FCSTD DOCUMENT  (FreeCAD 0.16RUnknown)
Label: Bioreactor_sketches_04
License: All rights reserved
LicenseURL: http://en.wikipedia.org/wiki/All_rights_reserved
objects: Sketcher::SketchObject×15, Spreadsheet::Sheet×1
note: 15 computed .brp shape members not serialized (recipe doc carries the construction recipe); baked Part::Feature solids carry a one-line shape summary decoded from their .brp

FEATURE [Spreadsheet::Sheet] Spreadsheet  label="prefs001"
  cells = A1=PCBHeated; B1(pcbheated)=214; C1=mm; D1=name=pcbheated; A2=Plexi thickness main; B2(plexi)=6; C2=mm; D2=name=plexi; A3=Plexi thickness LCD top; B3(plexi_LCDcover)=4; C3=mm; D3=name=plexi_LCDcover; E3=WARNING: cut in different plexi thickness; A4=Grande Encoche; B4(big_encoche)=75; C4=mm; D4=name=big_encoche; A5=Boite_LCD_to_side; B5(lcd2side)=34.5; C5=mm; D5=name=lcd2side; A6=Length LCD box; B6(lcd_length)=70; C6=mm; D6=name=lcd_length; A7=Encoche LCD; B7(lcd_encoche)=47; C7=mm; D7=name=lcd_encoche; A8=Encoche side; B8(side_encoche)=16; C8=mm; D8=name=side_encoche; A9=Encoche LCD side; B9(LCDside_encoche)=14; C9=mm; D9=name=LCDside_encoche; A10=Encoche LCD bottom; B10(LCDbottom_encoche)=47; C10=mm; D10=name=LCDbottom_encoche; A11=Encoche LCD cover length; B11(LCDcover_encoche)=128; C11=mm; D11=name=LCDcover_encoche; A12=Box height; B12(box_height)=58; C12=mm; D12=name=box_height; A13=Encoche top; B13(top_encoche)=45; C13=mm; D13=name=top_encoche; A14=Plug opening width; B14(plug_width)=90; C14=mm; D14=name=plug_width; A15=Plug opening height; B15(plug_height)=25; C15=mm; D15=name=plug_height; A16=Radius Pump; B16(radius_pump)==29 / 2; C16=mm; D16=name=radius_pump; A17=Radius pump screw; B17(radius_pump_screw)==4 / 2; C17=mm; D17=name=radius_pump_screw; A18=Radius stepper; B18(radius_stepper)=6; C18=mm; D18=name=radius_stepper; A19=Radius stepper screw; B19(radius_stepper_screw)=2; C19=mm; D19=name=radius_stepper_screw; A20=Diagonal distance between stepper screws; B20(stepper_screw_dist1)=44; C20=mm; D20=name=stepper_screw_dist1; A21=Load cell opening length; B21(load_length)=55; C21=mm; D21=name=load_length; A22=Load cell opening width; B22(load_width)=17; C22=mm; D22=name=load_width; A23=Radius load cell screw; B23(load_screw)=2.5; C23=mm; D23=name=load_screw; A24=Distance between load position screw; B24(load_dist1)=10; C24=mm; D24=name=load_dist1; E24=value for smaller loading cell = 5; A25=Distance between stepper & loading points; B25(load_dist_point)=67.5; C25=mm; D25=name=load_dist_point; A26=Distance load screw opening; B26(load_dist2)=7; C26=mm; D26=name=load_dist2; A27=Distance screw weighting; B27(load_dist_weight)==66 + 2.5; C27=mm; D27=name=load_dist_weight; E27=value for smaller loading cell = 62.5; A28=Load cell opening border distance; B28(load_border)=20; C28=mm; D28=name=load_border; A29=USB entry length; B29(usb_length)=9; C29=mm; D29=name=usb_length; A30=USB entry height; B30(usb_height)=5; C30=mm; D30=name=usb_height; A31=Ethernet entry length; B31(ethernet_length)=15; C31=mm; D31=name=ethernet_length; A32=Ethernet entry height; B32(ethernet_height)=16; C32=mm; D32=name=ethernet_height; A33=Power entry length; B33(power_length)=10; C33=mm; D33=name=power_length; A34=Power entry height; B34(power_height)=12.5; C34=mm; D34=name=power_height
FEATURE [Sketcher::SketchObject] Sketch  label="BASE_JUPE_MALE"
  expr: Constraints[17] = prefs001.pcbheated
  expr: Constraints[18] = prefs001.plexi * 2
  expr: Constraints[20] = prefs001.plexi * 2
  expr: Constraints[33] = prefs001.plexi * 2
  expr: Constraints[23] = prefs001.plexi * 2
  expr: Constraints[22] = prefs001.plexi
  expr: Constraints[24] = prefs001.plexi * 2
  expr: Constraints[35] = prefs001.pcbheated
  sketch-geometry (12):
    g0: LineSegment StartX=230 StartY=22 StartZ=0 EndX=236 EndY=22 EndZ=0
    g1: LineSegment StartX=236 StartY=22 StartZ=0 EndX=236 EndY=34 EndZ=0
    g2: LineSegment StartX=236 StartY=34 StartZ=0 EndX=230 EndY=34 EndZ=0
    g3: LineSegment StartX=230 StartY=34 StartZ=0 EndX=230 EndY=46 EndZ=0
    g4: LineSegment StartX=230 StartY=46 StartZ=0 EndX=16 EndY=46 EndZ=0
    g5: LineSegment StartX=16 StartY=46 StartZ=0 EndX=16 EndY=34 EndZ=0
    g6: LineSegment StartX=16 StartY=34 StartZ=0 EndX=10 EndY=34 EndZ=0
    g7: LineSegment StartX=10 StartY=34 StartZ=0 EndX=10 EndY=22 EndZ=0
    g8: LineSegment StartX=10 StartY=22 StartZ=0 EndX=16 EndY=22 EndZ=0
    g9: LineSegment StartX=16 StartY=22 StartZ=0 EndX=16 EndY=10 EndZ=0
    g10: LineSegment StartX=16 StartY=10 StartZ=0 EndX=230 EndY=10 EndZ=0
    g11: LineSegment StartX=230 StartY=10 StartZ=0 EndX=230 EndY=22 EndZ=0
  constraints (36):
    c: Horizontal(g0)
    c: Vertical(g1)
    c: Horizontal(g2)
    c: Vertical(g3)
    c: Horizontal(g4)
    c: Vertical(g5)
    c: Vertical(g7)
    c: DistanceX(g-1,g7) = 10
    c: Coincident(g7,g6)
    c: Coincident(g7,g8)
    c: Coincident(g0,g1)
    c: Coincident(g2,g1)
    c: Coincident(g2,g3)
    c: Coincident(g3,g4)
    c: Coincident(g5,g4)
    c: Coincident(g5,g6)
    c: Horizontal(g8)
    c: DistanceX(g4,g4) = 214
    c: DistanceY(g5,g5) = 12
    c: Horizontal(g6)
    c: DistanceY(g7,g7) = 12
    c: DistanceX(g8,g8) = 6
    c: DistanceX(g6,g6) = 6
    c: DistanceY(g3,g3) = 12
    c: DistanceY(g1,g1) = 12
    c: DistanceX(g2,g2) = 6
    c: Vertical(g9)
    c: Coincident(g9,g10)
    c: Horizontal(g10)
    c: Coincident(g10,g11)
    c: Coincident(g11,g0)
    c: Vertical(g11)
    c: Coincident(g9,g8)
    c: DistanceY(g9,g9) = 12
    c: DistanceY(g-1,g9) = 10
    c: DistanceX(g10,g10) = 214
FEATURE [Sketcher::SketchObject] Sketch001  label="BASE_JUPE_FEMELLE"
  expr: Constraints[37] = prefs001.plexi
  expr: Constraints[34] = prefs001.plexi * 2
  expr: Constraints[33] = prefs001.plexi * 2
  expr: Constraints[11] = prefs001.plexi
  expr: Constraints[36] = prefs001.plexi
  expr: Constraints[31] = prefs001.pcbheated + 2 * prefs001.plexi
  sketch-geometry (14):
    g0: LineSegment StartX=-236 StartY=27 StartZ=0 EndX=-230 EndY=27 EndZ=0
    g1: LineSegment StartX=-230 StartY=27 StartZ=0 EndX=-230 EndY=39 EndZ=0
    g2: LineSegment StartX=-230 StartY=39 StartZ=0 EndX=-236 EndY=39 EndZ=0
    g3: LineSegment StartX=-236 StartY=39 StartZ=0 EndX=-236 EndY=50 EndZ=0
    g4: LineSegment StartX=-196 StartY=90 StartZ=0 EndX=-50 EndY=90 EndZ=0
    g5: LineSegment StartX=-16 StartY=39 StartZ=0 EndX=-16 EndY=27 EndZ=0
    g6: ArcOfCircle CenterX=-50 CenterY=50 CenterZ=0 NormalX=0 NormalY=0 NormalZ=1 Radius=40 StartAngle=2.17158e-06 EndAngle=1.5708
    g7: ArcOfCircle CenterX=-196 CenterY=50 CenterZ=0 NormalX=0 NormalY=0 NormalZ=1 Radius=40 StartAngle=1.5708 EndAngle=3.14159
    g8: LineSegment StartX=-16 StartY=39 StartZ=0 EndX=-10 EndY=39 EndZ=0
    g9: LineSegment StartX=-10 StartY=50.0001 StartZ=0 EndX=-10 EndY=39 EndZ=0
    g10: LineSegment StartX=-236 StartY=27 StartZ=0 EndX=-236 EndY=15 EndZ=0
    g11: LineSegment StartX=-236 StartY=15 StartZ=0 EndX=-10 EndY=15 EndZ=0
    g12: LineSegment StartX=-10 StartY=15 StartZ=0 EndX=-10 EndY=27 EndZ=0
    g13: LineSegment StartX=-10 StartY=27 StartZ=0 EndX=-16 EndY=27 EndZ=0
  constraints (41):
    c: Horizontal(g0)
    c: Coincident(g0,g1)
    c: Vertical(g1)
    c: Coincident(g1,g2)
    c: Horizontal(g2)
    c: Coincident(g2,g3)
    c: Vertical(g3)
    c: Horizontal(g4)
    c: Vertical(g5)
    c: DistanceY(g1,g1) = 12
    c: DistanceY(g5,g5) = 12
    c: DistanceX(g2,g2) = 6
    c: DistanceX(g0,g0) = 6
    c: Tangent(g4,g6) = 1.5708
    c: Tangent(g3,g7) = 1.5708
    c: Tangent(g4,g7) = 1.5708
    c: Radius(g7) = 40
    c: Radius(g6) = 40
    c: Coincident(g8,g5)
    c: Horizontal(g8)
    c: Coincident(g9,g6)
    c: Coincident(g9,g8)
    c: Vertical(g9)
    c: Vertical(g10)
    c: Coincident(g10,g11)
    c: Horizontal(g11)
    c: Coincident(g11,g12)
    c: Vertical(g12)
    c: Coincident(g12,g13)
    c: Coincident(g13,g5)
    c: Horizontal(g13)
    c: DistanceX(g11,g11) = 226
    c: DistanceY(g10,g4) = 75
    c: DistanceY(g10,g10) = 12
    c: DistanceY(g12,g12) = 12
    c: Coincident(g0,g10)
    c: DistanceX(g8,g8) = 6
    c: DistanceX(g13,g13) = 6
    c: DistanceY(g-1,g11) = 15
    c: DistanceX(g11,g-1) = 10
    c: Tangent(g6,g9)
FEATURE [Sketcher::SketchObject] Sketch002  label="BASE_FOND"
  expr: Constraints[106] = 89.5 + 3.2
  expr: Constraints[83] = prefs001.lcd2side
  expr: Constraints[104] = 89.5 + 3.2
  expr: Constraints[97] = 51.5 + 3.2
  expr: Constraints[94] = (prefs001.pcbheated - 4 - prefs001.lcd_encoche - 2 * prefs001.lcd2side - 2 * prefs001.plexi) / 2
  expr: Constraints[91] = prefs001.plexi
  expr: Constraints[90] = prefs001.lcd_length / 2
  expr: Constraints[88] = prefs001.lcd_length / 2
  expr: Constraints[71] = prefs001.plexi
  expr: Constraints[57] = (prefs001.pcbheated - 4 - prefs001.big_encoche) / 2
  expr: Constraints[59] = prefs001.big_encoche
  expr: Constraints[65] = (prefs001.pcbheated - 4 - prefs001.big_encoche) / 2
  expr: Constraints[72] = prefs001.plexi
  expr: Constraints[64] = (prefs001.pcbheated - 4 - prefs001.big_encoche) / 2
  expr: Constraints[61] = prefs001.big_encoche
  expr: Constraints[117] = 9 + 6
  expr: Constraints[62] = (prefs001.pcbheated - 4 - prefs001.big_encoche) / 2
  expr: Constraints[89] = prefs001.lcd_length / 2
  expr: Constraints[66] = prefs001.big_encoche
  expr: Constraints[84] = prefs001.big_encoche
  expr: Constraints[68] = prefs001.plexi
  expr: Constraints[69] = prefs001.plexi
  expr: Constraints[73] = prefs001.plexi
  expr: Constraints[67] = prefs001.plexi
  expr: Constraints[85] = prefs001.plexi
  expr: Constraints[105] = 51.5 + 3.2
  expr: Constraints[82] = prefs001.lcd2side
  expr: Constraints[60] = (prefs001.pcbheated - 4 - prefs001.big_encoche) / 2
  expr: Constraints[93] = (prefs001.pcbheated - 4 - prefs001.lcd_encoche - 2 * prefs001.lcd2side - 2 * prefs001.plexi) / 2
  expr: Constraints[92] = prefs001.lcd_encoche
  expr: Constraints[87] = (prefs001.pcbheated - 4 - prefs001.big_encoche - 2 * prefs001.lcd2side) / 2
  expr: Constraints[58] = (prefs001.pcbheated - 4 - prefs001.big_encoche) / 2
  sketch-geometry (40):
    g0: LineSegment StartX=0 StartY=0 StartZ=0 EndX=0 EndY=-67.5 EndZ=0
    g1: LineSegment StartX=0 StartY=-67.5 StartZ=0 EndX=6 EndY=-67.5 EndZ=0
    g2: LineSegment StartX=6 StartY=-67.5 StartZ=0 EndX=6 EndY=-142.5 EndZ=0
    g3: LineSegment StartX=6 StartY=-142.5 StartZ=0 EndX=0 EndY=-142.5 EndZ=0
    g4: LineSegment StartX=0 StartY=-142.5 StartZ=0 EndX=0 EndY=-210 EndZ=0
    g5: LineSegment StartX=0 StartY=-210 StartZ=0 EndX=67.5 EndY=-210 EndZ=0
    g6: LineSegment StartX=67.5 StartY=-210 StartZ=0 EndX=67.5 EndY=-204 EndZ=0
    g7: LineSegment StartX=67.5 StartY=-204 StartZ=0 EndX=142.5 EndY=-204 EndZ=0
    g8: LineSegment StartX=142.5 StartY=-204 StartZ=0 EndX=142.5 EndY=-210 EndZ=0
    g9: LineSegment StartX=142.5 StartY=-210 StartZ=0 EndX=210 EndY=-210 EndZ=0
    g10: LineSegment StartX=210 StartY=-210 StartZ=0 EndX=210 EndY=-175.5 EndZ=0
    g11: LineSegment StartX=210 StartY=-175.5 StartZ=0 EndX=245 EndY=-175.5 EndZ=0
    g12: LineSegment StartX=245 StartY=-175.5 StartZ=0 EndX=245 EndY=-169.5 EndZ=0
    g13: LineSegment StartX=245 StartY=-169.5 StartZ=0 EndX=280 EndY=-169.5 EndZ=0
    g14: LineSegment StartX=280 StartY=-169.5 StartZ=0 EndX=280 EndY=-128.5 EndZ=0
    g15: LineSegment StartX=280 StartY=-128.5 StartZ=0 EndX=274 EndY=-128.5 EndZ=0
    g16: LineSegment StartX=274 StartY=-128.5 StartZ=0 EndX=274 EndY=-81.5 EndZ=0
    g17: LineSegment StartX=274 StartY=-81.5 StartZ=0 EndX=280 EndY=-81.5 EndZ=0
    g18: LineSegment StartX=280 StartY=-81.5 StartZ=0 EndX=280 EndY=-40.5 EndZ=0
    g19: LineSegment StartX=280 StartY=-40.5 StartZ=0 EndX=245 EndY=-40.5 EndZ=0
    g20: LineSegment StartX=245 StartY=-40.5 StartZ=0 EndX=245 EndY=-34.5 EndZ=0
    g21: LineSegment StartX=245 StartY=-34.5 StartZ=0 EndX=210 EndY=-34.5 EndZ=0
    g22: LineSegment StartX=210 StartY=-34.5 StartZ=0 EndX=210 EndY=0 EndZ=0
    g23: LineSegment StartX=210 StartY=0 StartZ=0 EndX=142.5 EndY=0 EndZ=0
    g24: LineSegment StartX=142.5 StartY=0 StartZ=0 EndX=142.5 EndY=-6 EndZ=0
    g25: LineSegment StartX=142.5 StartY=-6 StartZ=0 EndX=67.5 EndY=-6 EndZ=0
    g26: LineSegment StartX=67.5 StartY=-6 StartZ=0 EndX=67.5 EndY=0 EndZ=0
    g27: LineSegment StartX=67.5 StartY=0 StartZ=0 EndX=0 EndY=0 EndZ=0
    g28: LineSegment StartX=204 StartY=-67.5 StartZ=0 EndX=210 EndY=-67.5 EndZ=0
    g29: LineSegment StartX=210 StartY=-67.5 StartZ=0 EndX=210 EndY=-142.5 EndZ=0
    g30: LineSegment StartX=210 StartY=-142.5 StartZ=0 EndX=204 EndY=-142.5 EndZ=0
    g31: LineSegment StartX=204 StartY=-142.5 StartZ=0 EndX=204 EndY=-67.5 EndZ=0
    g32: Circle CenterX=269 CenterY=-165.5 CenterZ=0 NormalX=0 NormalY=0 NormalZ=1 Radius=1.6
    g33: Circle CenterX=214.3 CenterY=-165.5 CenterZ=0 NormalX=0 NormalY=0 NormalZ=1 Radius=1.6
    g34: Circle CenterX=214.3 CenterY=-72.8 CenterZ=0 NormalX=0 NormalY=0 NormalZ=1 Radius=1.6
    g35: Circle CenterX=269 CenterY=-72.8 CenterZ=0 NormalX=0 NormalY=0 NormalZ=1 Radius=1.6
    g36: Circle CenterX=15 CenterY=-190 CenterZ=0 NormalX=0 NormalY=0 NormalZ=1 Radius=1.6
    g37: Circle CenterX=88 CenterY=-190 CenterZ=0 NormalX=0 NormalY=0 NormalZ=1 Radius=1.6
    g38: Circle CenterX=88 CenterY=-96 CenterZ=0 NormalX=0 NormalY=0 NormalZ=1 Radius=1.6
    g39: Circle CenterX=15 CenterY=-96 CenterZ=0 NormalX=0 NormalY=0 NormalZ=1 Radius=1.6
  constraints (119):
    c: Coincident(g-1,g0)
    c: Vertical(g0)
    c: Coincident(g0,g1)
    c: Horizontal(g1)
    c: Coincident(g1,g2)
    c: Vertical(g2)
    c: Coincident(g2,g3)
    c: PointOnObject(g3,g-2)
    c: Horizontal(g3)
    c: Coincident(g3,g4)
    c: Vertical(g4)
    c: Coincident(g4,g5)
    c: Horizontal(g5)
    c: Coincident(g5,g6)
    c: Vertical(g6)
    c: Coincident(g6,g7)
    c: Horizontal(g7)
    c: Coincident(g7,g8)
    c: Vertical(g8)
    c: Coincident(g8,g9)
    c: Horizontal(g9)
    c: Coincident(g9,g10)
    c: Vertical(g10)
    c: Coincident(g10,g11)
    c: Horizontal(g11)
    c: Coincident(g11,g12)
    c: Vertical(g12)
    c: Coincident(g12,g13)
    c: Horizontal(g13)
    c: Coincident(g13,g14)
    c: Vertical(g14)
    c: Coincident(g14,g15)
    c: Horizontal(g15)
    c: Coincident(g15,g16)
    c: Vertical(g16)
    c: Coincident(g16,g17)
    c: Horizontal(g17)
    c: Coincident(g17,g18)
    c: Vertical(g18)
    c: Coincident(g18,g19)
    c: Horizontal(g19)
    c: Coincident(g19,g20)
    c: Vertical(g20)
    c: Coincident(g20,g21)
    c: Horizontal(g21)
    c: Coincident(g21,g22)
    c: Vertical(g22)
    c: Coincident(g22,g23)
    c: Horizontal(g23)
    c: Coincident(g23,g24)
    c: Coincident(g24,g25)
    c: Horizontal(g25)
    c: Coincident(g25,g26)
    c: Vertical(g26)
    c: Coincident(g26,g27)
    c: Coincident(g27,g0)
    c: Horizontal(g27)
    c: DistanceY(g0,g0) = 67.5
    c: DistanceY(g4,g4) = 67.5
    c: DistanceY(g2,g2) = 75
    c: DistanceX(g5,g5) = 67.5
    c: DistanceX(g7,g7) = 75
    c: DistanceX(g9,g9) = 67.5
    c: Vertical(g24)
    c: DistanceX(g23,g23) = 67.5
    c: DistanceX(g27,g27) = 67.5
    c: DistanceX(g25,g25) = 75
    c: DistanceY(g8,g8) = 6
    c: DistanceY(g6,g6) = 6
    c: DistanceX(g3,g3) = 6
    c: DistanceY(g20,g20) = 6
    c: DistanceY(g12,g12) = 6
    c: DistanceX(g15,g15) = 6
    c: DistanceX(g17,g17) = 6
    c: Coincident(g28,g29)
    c: Coincident(g29,g30)
    c: Coincident(g30,g31)
    c: Coincident(g31,g28)
    c: Horizontal(g28)
    c: Horizontal(g30)
    c: Vertical(g29)
    c: Vertical(g31)
    c: DistanceY(g22,g22) = 34.5
    c: DistanceY(g10,g10) = 34.5
    c: DistanceY(g31,g31) = 75
    c: DistanceX(g28,g28) = 6
    c: DistanceX(g28,g21) = 0
    c: DistanceY(g28,g21) = 33
    c: DistanceX(g21,g21) = 35
    c: DistanceX(g19,g19) = 35
    c: DistanceX(g11,g11) = 35
    c: DistanceY(g24,g24) = 6
    c: DistanceY(g16,g16) = 47
    c: DistanceY(g18,g18) = 41
    c: DistanceY(g14,g14) = 41
    c: Radius(g32) = 1.6
    c: Radius(g33) = 1.6
    c: DistanceX(g33,g32) = 54.7
    c: DistanceY(g33,g32) = 0
    c: DistanceY(g13,g32) = 4
    c: DistanceX(g32,g13) = 11
    c: Radius(g35) = 1.6
    c: Radius(g34) = 1.6
    c: DistanceX(g35,g32) = 0
    c: DistanceY(g32,g35) = 92.7
    c: DistanceX(g34,g35) = 54.7
    c: DistanceY(g33,g34) = 92.7
    c: Radius(g39) = 1.6
    c: Radius(g38) = 1.6
    c: Radius(g36) = 1.6
    c: Radius(g37) = 1.6
    c: DistanceY(g36,g37) = 0
    c: DistanceY(g38,g39) = 0
    c: DistanceY(g37,g38) = 94
    c: DistanceX(g39,g38) = 73
    c: DistanceX(g39,g36) = 0
    c: DistanceX(g37,g38) = 0
    c: DistanceX(g4,g36) = 15
    c: DistanceY(g4,g36) = 20
FEATURE [Sketcher::SketchObject] Sketch003  label="BASE_PAROI_FEMELLE_SIDE"
  expr: Constraints[70] = (prefs001.pcbheated - 4 - 3 * prefs001.top_encoche) / 2
  expr: Constraints[78] = prefs001.radius_pump_screw
  expr: Constraints[58] = prefs001.plexi
  expr: Constraints[52] = (prefs001.box_height - prefs001.side_encoche) / 2
  expr: Constraints[73] = prefs001.radius_pump_screw
  expr: Constraints[79] = prefs001.radius_pump
  expr: Constraints[74] = prefs001.radius_pump
  expr: Constraints[71] = prefs001.pcbheated + 10
  expr: Constraints[68] = prefs001.top_encoche
  expr: Constraints[67] = prefs001.top_encoche
  expr: Constraints[66] = prefs001.plexi
  expr: Constraints[65] = prefs001.plexi
  expr: Constraints[54] = (prefs001.box_height - prefs001.side_encoche) / 2
  expr: Constraints[61] = prefs001.plexi
  expr: Constraints[64] = prefs001.plexi
  expr: Constraints[72] = prefs001.radius_pump_screw
  expr: Constraints[63] = prefs001.plexi
  expr: Constraints[62] = prefs001.plexi
  expr: Constraints[55] = prefs001.side_encoche
  expr: Constraints[59] = prefs001.plexi
  expr: Constraints[53] = (prefs001.box_height - prefs001.side_encoche) / 2
  expr: Constraints[51] = (prefs001.box_height - prefs001.side_encoche) / 2
  expr: Constraints[49] = (prefs001.pcbheated - 4 - prefs001.big_encoche) / 2
  expr: Constraints[69] = prefs001.top_encoche
  expr: Constraints[60] = prefs001.plexi
  expr: Constraints[50] = prefs001.side_encoche
  expr: Constraints[46] = prefs001.big_encoche
  sketch-geometry (30):
    g0: LineSegment StartX=0 StartY=-224 StartZ=0 EndX=67.5 EndY=-224 EndZ=0
    g1: LineSegment StartX=67.5 StartY=-224 StartZ=0 EndX=67.5 EndY=-218 EndZ=0
    g2: LineSegment StartX=67.5 StartY=-218 StartZ=0 EndX=142.5 EndY=-218 EndZ=0
    g3: LineSegment StartX=142.5 StartY=-218 StartZ=0 EndX=142.5 EndY=-224 EndZ=0
    g4: LineSegment StartX=142.5 StartY=-224 StartZ=0 EndX=210 EndY=-224 EndZ=0
    g5: LineSegment StartX=210 StartY=-224 StartZ=0 EndX=210 EndY=-245 EndZ=0
    g6: LineSegment StartX=210 StartY=-245 StartZ=0 EndX=204 EndY=-245 EndZ=0
    g7: LineSegment StartX=204 StartY=-245 StartZ=0 EndX=204 EndY=-261 EndZ=0
    g8: LineSegment StartX=204 StartY=-261 StartZ=0 EndX=210 EndY=-261 EndZ=0
    g9: LineSegment StartX=210 StartY=-261 StartZ=0 EndX=210 EndY=-282 EndZ=0
    g10: LineSegment StartX=210 StartY=-282 StartZ=0 EndX=172.5 EndY=-282 EndZ=0
    g11: LineSegment StartX=172.5 StartY=-282 StartZ=0 EndX=172.5 EndY=-288 EndZ=0
    g12: LineSegment StartX=172.5 StartY=-288 StartZ=0 EndX=127.5 EndY=-288 EndZ=0
    g13: LineSegment StartX=127.5 StartY=-288 StartZ=0 EndX=127.5 EndY=-282 EndZ=0
    g14: LineSegment StartX=127.5 StartY=-282 StartZ=0 EndX=82.5 EndY=-282 EndZ=0
    g15: LineSegment StartX=82.5 StartY=-282 StartZ=0 EndX=82.5 EndY=-288 EndZ=0
    g16: LineSegment StartX=82.5 StartY=-288 StartZ=0 EndX=37.5 EndY=-288 EndZ=0
    g17: LineSegment StartX=37.5 StartY=-288 StartZ=0 EndX=37.5 EndY=-282 EndZ=0
    g18: LineSegment StartX=37.5 StartY=-282 StartZ=0 EndX=0 EndY=-282 EndZ=0
    g19: LineSegment StartX=0 StartY=-282 StartZ=0 EndX=0 EndY=-261 EndZ=0
    g20: LineSegment StartX=0 StartY=-261 StartZ=0 EndX=6 EndY=-261 EndZ=0
    g21: LineSegment StartX=6 StartY=-261 StartZ=0 EndX=6 EndY=-245 EndZ=0
    g22: LineSegment StartX=6 StartY=-245 StartZ=0 EndX=0 EndY=-245 EndZ=0
    g23: LineSegment StartX=0 StartY=-245 StartZ=0 EndX=0 EndY=-224 EndZ=0
    g24: Circle CenterX=37 CenterY=-252 CenterZ=0 NormalX=0 NormalY=0 NormalZ=1 Radius=14.5
    g25: Circle CenterX=20 CenterY=-233.943 CenterZ=0 NormalX=0 NormalY=0 NormalZ=1 Radius=2
    g26: Circle CenterX=54 CenterY=-270.057 CenterZ=0 NormalX=0 NormalY=0 NormalZ=1 Radius=2
    g27: Circle CenterX=114 CenterY=-270.057 CenterZ=0 NormalX=0 NormalY=0 NormalZ=1 Radius=2
    g28: Circle CenterX=97 CenterY=-252 CenterZ=0 NormalX=0 NormalY=0 NormalZ=1 Radius=14.5
    g29: Circle CenterX=80 CenterY=-233.943 CenterZ=0 NormalX=0 NormalY=0 NormalZ=1 Radius=2
  constraints (88):
    c: Horizontal(g0)
    c: Coincident(g0,g1)
    c: Vertical(g1)
    c: Coincident(g1,g2)
    c: Horizontal(g2)
    c: Coincident(g2,g3)
    c: Vertical(g3)
    c: Coincident(g3,g4)
    c: Horizontal(g4)
    c: Coincident(g4,g5)
    c: Vertical(g5)
    c: Coincident(g5,g6)
    c: Horizontal(g6)
    c: Coincident(g6,g7)
    c: Vertical(g7)
    c: Coincident(g7,g8)
    c: Horizontal(g8)
    c: Coincident(g8,g9)
    c: Vertical(g9)
    c: Coincident(g9,g10)
    c: Horizontal(g10)
    c: Coincident(g10,g11)
    c: Coincident(g11,g12)
    c: Horizontal(g12)
    c: Coincident(g12,g13)
    c: Vertical(g13)
    c: Coincident(g13,g14)
    c: Horizontal(g14)
    c: Coincident(g14,g15)
    c: Vertical(g15)
    c: Coincident(g15,g16)
    c: Horizontal(g16)
    c: Coincident(g16,g17)
    c: Coincident(g17,g18)
    c: Horizontal(g18)
    c: Coincident(g18,g19)
    c: Vertical(g19)
    c: Coincident(g19,g20)
    c: Horizontal(g20)
    c: Coincident(g20,g21)
    c: Vertical(g21)
    c: Coincident(g21,g22)
    c: Horizontal(g22)
    c: Coincident(g22,g23)
    c: Vertical(g23)
    c: Coincident(g0,g23)
    c: DistanceX(g2,g2) = 75
    c: DistanceX(g0,g0) = 67.5
    c: DistanceX(g-1,g0) = 0
    c: DistanceX(g4,g4) = 67.5
    c: DistanceY(g21,g21) = 16
    c: DistanceY(g23,g23) = 21
    c: DistanceY(g19,g19) = 21
    c: DistanceY(g5,g5) = 21
    c: DistanceY(g9,g9) = 21
    c: DistanceY(g7,g7) = 16
    c: Vertical(g17)
    c: Vertical(g11)
    c: DistanceX(g22,g22) = 6
    c: DistanceX(g20,g20) = 6
    c: DistanceY(g1,g1) = 6
    c: DistanceY(g3,g3) = 6
    c: DistanceX(g6,g6) = 6
    c: DistanceX(g8,g8) = 6
    c: DistanceY(g11,g11) = 6
    c: DistanceY(g13,g13) = 6
    c: DistanceY(g15,g15) = 6
    c: DistanceX(g16,g16) = 45
    c: DistanceX(g12,g12) = 45
    c: DistanceX(g14,g14) = 45
    c: DistanceX(g18,g18) = 37.5
    c: DistanceY(g0,g-1) = 224
    c: Radius(g25) = 2
    c: Radius(g26) = 2
    c: Radius(g24) = 14.5
    c: Symmetric(g26,g25,g24)
    c: Distance(g25,g24) = 24.8
    c: Radius(g29) = 2
    c: Radius(g27) = 2
    c: Radius(g28) = 14.5
    c: Symmetric(g27,g29,g28)
    c: Distance(g29,g28) = 24.8
    c: DistanceX(g0,g25) = 20
    c: DistanceY(g24,g0) = 28
    c: DistanceY(g28,g0) = 28
    c: DistanceX(g24,g28) = 60
    c: DistanceX(g26,g27) = 60
    c: DistanceX(g0,g24) = 37
FEATURE [Sketcher::SketchObject] Sketch005  label="BASE_PAROI_MALE_BACK"
  expr: Constraints[65] = prefs001.plexi
  expr: Constraints[61] = (prefs001.pcbheated - 4 - 3 * prefs001.top_encoche - 2 * prefs001.plexi) / 2
  expr: Constraints[54] = prefs001.top_encoche
  expr: Constraints[64] = prefs001.plexi
  expr: Constraints[63] = prefs001.plexi
  expr: Constraints[62] = prefs001.plexi
  expr: Constraints[48] = (prefs001.pcbheated - 4 - prefs001.big_encoche - 2 * prefs001.plexi) / 2
  expr: Constraints[67] = prefs001.plexi
  expr: Constraints[56] = (prefs001.box_height - prefs001.side_encoche) / 2
  expr: Constraints[57] = (prefs001.box_height - prefs001.side_encoche) / 2
  expr: Constraints[66] = prefs001.plexi
  expr: Constraints[51] = prefs001.side_encoche
  expr: Constraints[49] = (prefs001.pcbheated - 4 - prefs001.big_encoche - 2 * prefs001.plexi) / 2
  expr: Constraints[69] = prefs001.plexi
  expr: Constraints[68] = prefs001.plexi
  expr: Constraints[58] = (prefs001.box_height - prefs001.side_encoche) / 2
  expr: Constraints[82] = prefs001.plexi
  expr: Constraints[50] = prefs001.side_encoche
  expr: Constraints[60] = (prefs001.pcbheated - 4 - 3 * prefs001.top_encoche - 2 * prefs001.plexi) / 2
  expr: Constraints[53] = prefs001.top_encoche
  expr: Constraints[55] = prefs001.top_encoche
  expr: Constraints[59] = (prefs001.box_height - prefs001.side_encoche) / 2
  expr: Constraints[43] = prefs001.big_encoche
  sketch-geometry (28):
    g0: LineSegment StartX=-10 StartY=-208 StartZ=0 EndX=-31 EndY=-208 EndZ=0
    g1: LineSegment StartX=-31 StartY=-208 StartZ=0 EndX=-31 EndY=-214 EndZ=0
    g2: LineSegment StartX=-31 StartY=-214 StartZ=0 EndX=-47 EndY=-214 EndZ=0
    g3: LineSegment StartX=-47 StartY=-214 StartZ=0 EndX=-47 EndY=-208 EndZ=0
    g4: LineSegment StartX=-47 StartY=-208 StartZ=0 EndX=-68 EndY=-208 EndZ=0
    g5: LineSegment StartX=-68 StartY=-208 StartZ=0 EndX=-68 EndY=-176.5 EndZ=0
    g6: LineSegment StartX=-68 StartY=-176.5 StartZ=0 EndX=-74 EndY=-176.5 EndZ=0
    g7: LineSegment StartX=-74 StartY=-176.5 StartZ=0 EndX=-74 EndY=-131.5 EndZ=0
    g8: LineSegment StartX=-74 StartY=-131.5 StartZ=0 EndX=-68 EndY=-131.5 EndZ=0
    g9: LineSegment StartX=-68 StartY=-131.5 StartZ=0 EndX=-68 EndY=-86.5 EndZ=0
    g10: LineSegment StartX=-68 StartY=-86.5 StartZ=0 EndX=-74 EndY=-86.5 EndZ=0
    g11: LineSegment StartX=-74 StartY=-86.5 StartZ=0 EndX=-74 EndY=-41.5 EndZ=0
    g12: LineSegment StartX=-74 StartY=-41.5 StartZ=0 EndX=-68 EndY=-41.5 EndZ=0
    g13: LineSegment StartX=-68 StartY=-41.5 StartZ=0 EndX=-68 EndY=-10 EndZ=0
    g14: LineSegment StartX=-47 StartY=-10 StartZ=0 EndX=-47 EndY=-4 EndZ=0
    g15: LineSegment StartX=-47 StartY=-4 StartZ=0 EndX=-31 EndY=-4 EndZ=0
    g16: LineSegment StartX=-31 StartY=-4 StartZ=0 EndX=-31 EndY=-10 EndZ=0
    g17: LineSegment StartX=-68 StartY=-10 StartZ=0 EndX=-47 EndY=-10 EndZ=0
    g18: LineSegment StartX=-31 StartY=-10 StartZ=0 EndX=-10 EndY=-10 EndZ=0
    g19: LineSegment StartX=-10 StartY=-10 StartZ=0 EndX=-10 EndY=-71.5 EndZ=0
    g20: LineSegment StartX=-10 StartY=-71.5 StartZ=0 EndX=-4 EndY=-71.5 EndZ=0
    g21: LineSegment StartX=-4 StartY=-71.5 StartZ=0 EndX=-4 EndY=-146.5 EndZ=0
    g22: LineSegment StartX=-4 StartY=-146.5 StartZ=0 EndX=-10 EndY=-146.5 EndZ=0
    g23: LineSegment StartX=-10 StartY=-146.5 StartZ=0 EndX=-10 EndY=-208 EndZ=0
    g24: LineSegment StartX=-41 StartY=-30 StartZ=0 EndX=-16 EndY=-30 EndZ=0
    g25: LineSegment StartX=-16 StartY=-30 StartZ=0 EndX=-16 EndY=-120 EndZ=0
    g26: LineSegment StartX=-16 StartY=-120 StartZ=0 EndX=-41 EndY=-120 EndZ=0
    g27: LineSegment StartX=-41 StartY=-120 StartZ=0 EndX=-41 EndY=-30 EndZ=0
  constraints (84):
    c: Horizontal(g0)
    c: Coincident(g0,g1)
    c: Vertical(g1)
    c: Coincident(g1,g2)
    c: Horizontal(g2)
    c: Coincident(g2,g3)
    c: Vertical(g3)
    c: Coincident(g3,g4)
    c: Horizontal(g4)
    c: Coincident(g4,g5)
    c: Vertical(g5)
    c: Coincident(g5,g6)
    c: Horizontal(g6)
    c: Coincident(g6,g7)
    c: Vertical(g7)
    c: Coincident(g7,g8)
    c: Horizontal(g8)
    c: Coincident(g8,g9)
    c: Vertical(g9)
    c: Coincident(g9,g10)
    c: Horizontal(g10)
    c: Coincident(g10,g11)
    c: Vertical(g11)
    c: Coincident(g11,g12)
    c: Coincident(g12,g13)
    c: Vertical(g13)
    c: Vertical(g14)
    c: Coincident(g14,g15)
    c: Horizontal(g15)
    c: Coincident(g15,g16)
    c: Vertical(g16)
    c: Coincident(g17,g13)
    c: Coincident(g17,g14)
    c: Coincident(g18,g16)
    c: Horizontal(g18)
    c: Vertical(g19)
    c: Horizontal(g20)
    c: Coincident(g21,g20)
    c: Vertical(g21)
    c: Horizontal(g22)
    c: Coincident(g23,g0)
    c: Vertical(g23)
    c: Horizontal(g17)
    c: DistanceY(g21,g21) = 75
    c: Coincident(g22,g21)
    c: Coincident(g23,g22)
    c: Coincident(g20,g19)
    c: Coincident(g18,g19)
    c: DistanceY(g19,g19) = 61.5
    c: DistanceY(g23,g23) = 61.5
    c: DistanceX(g15,g15) = 16
    c: DistanceX(g2,g2) = 16
    c: Horizontal(g12)
    c: DistanceY(g11,g11) = 45
    c: DistanceY(g9,g9) = 45
    c: DistanceY(g7,g7) = 45
    c: DistanceX(g18,g18) = 21
    c: DistanceX(g17,g17) = 21
    c: DistanceX(g4,g4) = 21
    c: DistanceX(g0,g0) = 21
    c: DistanceY(g13,g13) = 31.5
    c: DistanceY(g5,g5) = 31.5
    c: DistanceY(g14,g14) = 6
    c: DistanceY(g16,g16) = 6
    c: DistanceX(g12,g12) = 6
    c: DistanceX(g10,g10) = 6
    c: DistanceX(g20,g20) = 6
    c: DistanceX(g8,g8) = 6
    c: DistanceX(g6,g6) = 6
    c: DistanceY(g3,g3) = 6
    c: DistanceY(g18,g-1) = 10
    c: DistanceX(g18,g-1) = 10
    c: Coincident(g24,g25)
    c: Coincident(g25,g26)
    c: Coincident(g26,g27)
    c: Coincident(g27,g24)
    c: Horizontal(g24)
    c: Horizontal(g26)
    c: Vertical(g25)
    c: Vertical(g27)
    c: DistanceY(g25,g25) = 90
    c: DistanceX(g26,g26) = 25
    c: DistanceX(g24,g18) = 6
    c: DistanceY(g24,g18) = 20
FEATURE [Sketcher::SketchObject] Sketch006  label="BASE_INTERMEDIAIRE"
  expr: Constraints[184] = prefs001.load_width / 2
  expr: Constraints[102] = (prefs001.pcbheated - 4 - 3 * prefs001.top_encoche) / 2
  expr: Constraints[171] = prefs001.load_width / 2
  expr: Constraints[131] = (prefs001.pcbheated - 4) / 2
  expr: Constraints[164] = prefs001.load_border * 1.5
  expr: Constraints[90] = prefs001.plexi
  expr: Constraints[162] = prefs001.load_length
  expr: Constraints[78] = prefs001.top_encoche
  expr: Constraints[104] = (prefs001.pcbheated - 4 - 3 * prefs001.top_encoche) / 2
  expr: Constraints[163] = prefs001.load_width
  expr: Constraints[91] = prefs001.plexi
  expr: Constraints[169] = prefs001.load_width / 2
  expr: Constraints[88] = prefs001.plexi
  expr: Constraints[74] = prefs001.top_encoche
  expr: Constraints[86] = prefs001.plexi
  expr: Constraints[127] = prefs001.load_width
  expr: Constraints[95] = prefs001.plexi
  expr: Constraints[150] = prefs001.load_border * 1.5
  expr: Constraints[112] = prefs001.radius_stepper_screw
  expr: Constraints[99] = prefs001.plexi
  expr: Constraints[181] = prefs001.load_width / 2
  expr: Constraints[172] = prefs001.load_dist_weight
  expr: Constraints[183] = prefs001.load_width / 2
  expr: Constraints[166] = prefs001.load_screw
  expr: Constraints[110] = prefs001.radius_stepper_screw
  expr: Constraints[182] = prefs001.load_width / 2
  expr: Constraints[167] = prefs001.load_dist1 + 2 * prefs001.load_screw
  expr: Constraints[148] = prefs001.load_length
  expr: Constraints[82] = prefs001.top_encoche
  expr: Constraints[149] = prefs001.load_width
  expr: Constraints[100] = (prefs001.pcbheated - 4 - 3 * prefs001.top_encoche) / 2
  expr: Constraints[134] = prefs001.load_border
  expr: Constraints[109] = prefs001.radius_stepper_screw
  expr: Constraints[145] = prefs001.load_screw
  expr: Constraints[108] = prefs001.radius_stepper
  expr: Constraints[146] = prefs001.load_screw
  expr: Constraints[103] = (prefs001.pcbheated - 4 - 3 * prefs001.top_encoche) / 2
  expr: Constraints[111] = prefs001.radius_stepper_screw
  expr: Constraints[97] = prefs001.plexi
  expr: Constraints[98] = prefs001.plexi
  expr: Constraints[89] = prefs001.plexi
  expr: Constraints[84] = prefs001.plexi
  expr: Constraints[81] = prefs001.top_encoche
  expr: Constraints[176] = (100 - prefs001.top_encoche) / 2
  expr: Constraints[170] = prefs001.load_width / 2
  expr: Constraints[77] = prefs001.top_encoche
  expr: Constraints[79] = prefs001.top_encoche
  expr: Constraints[83] = prefs001.top_encoche
  expr: Constraints[73] = prefs001.top_encoche
  expr: Constraints[75] = prefs001.top_encoche
  expr: Constraints[101] = (prefs001.pcbheated - 4 - 3 * prefs001.top_encoche) / 2
  expr: Constraints[132] = prefs001.load_screw
  expr: Constraints[147] = prefs001.load_dist1 + 2 * prefs001.load_screw
  expr: Constraints[85] = prefs001.plexi
  expr: Constraints[118] = (prefs001.pcbheated - 4) / 2
  expr: Constraints[173] = prefs001.stepper_screw_dist1
  expr: Constraints[116] = prefs001.stepper_screw_dist1
  expr: Constraints[152] = prefs001.load_width / 2
  expr: Constraints[180] = prefs001.stepper_screw_dist1 / sqrt(2)
  expr: Constraints[96] = prefs001.plexi
  expr: Constraints[93] = prefs001.plexi
  expr: Constraints[178] = (100 - prefs001.top_encoche) / 2
  expr: Constraints[87] = prefs001.plexi
  expr: Constraints[92] = prefs001.plexi
  expr: Constraints[136] = prefs001.load_dist_weight
  expr: Constraints[80] = prefs001.top_encoche
  expr: Constraints[94] = prefs001.plexi
  expr: Constraints[133] = prefs001.load_screw
  expr: Constraints[130] = prefs001.load_length
  expr: Constraints[76] = prefs001.top_encoche
  expr: Constraints[117] = (prefs001.pcbheated - 4) / 2
  expr: Constraints[72] = prefs001.top_encoche
  expr: Constraints[128] = prefs001.load_width / 2
  sketch-geometry (64):
    g0: LineSegment StartX=-295 StartY=-5 StartZ=0 EndX=-257.5 EndY=-5 EndZ=0
    g1: LineSegment StartX=-257.5 StartY=-5 StartZ=0 EndX=-257.5 EndY=-11 EndZ=0
    g2: LineSegment StartX=-257.5 StartY=-11 StartZ=0 EndX=-212.5 EndY=-11 EndZ=0
    g3: LineSegment StartX=-212.5 StartY=-11 StartZ=0 EndX=-212.5 EndY=-5 EndZ=0
    g4: LineSegment StartX=-212.5 StartY=-5 StartZ=0 EndX=-167.5 EndY=-5 EndZ=0
    g5: LineSegment StartX=-167.5 StartY=-5 StartZ=0 EndX=-167.5 EndY=-11 EndZ=0
    g6: LineSegment StartX=-167.5 StartY=-11 StartZ=0 EndX=-122.5 EndY=-11 EndZ=0
    g7: LineSegment StartX=-122.5 StartY=-11 StartZ=0 EndX=-122.5 EndY=-5 EndZ=0
    g8: LineSegment StartX=-122.5 StartY=-5 StartZ=0 EndX=-85 EndY=-5 EndZ=0
    g9: LineSegment StartX=-85 StartY=-5 StartZ=0 EndX=-85 EndY=-42.5 EndZ=0
    g10: LineSegment StartX=-85 StartY=-42.5 StartZ=0 EndX=-91 EndY=-42.5 EndZ=0
    g11: LineSegment StartX=-91 StartY=-42.5 StartZ=0 EndX=-91 EndY=-87.5 EndZ=0
    g12: LineSegment StartX=-91 StartY=-87.5 StartZ=0 EndX=-85 EndY=-87.5 EndZ=0
    g13: LineSegment StartX=-85 StartY=-87.5 StartZ=0 EndX=-85 EndY=-132.5 EndZ=0
    g14: LineSegment StartX=-85 StartY=-132.5 StartZ=0 EndX=-91 EndY=-132.5 EndZ=0
    g15: LineSegment StartX=-91 StartY=-132.5 StartZ=0 EndX=-91 EndY=-177.5 EndZ=0
    g16: LineSegment StartX=-91 StartY=-177.5 StartZ=0 EndX=-85 EndY=-177.5 EndZ=0
    g17: LineSegment StartX=-85 StartY=-177.5 StartZ=0 EndX=-85 EndY=-215 EndZ=0
    g18: LineSegment StartX=-85 StartY=-215 StartZ=0 EndX=-122.5 EndY=-215 EndZ=0
    g19: LineSegment StartX=-122.5 StartY=-215 StartZ=0 EndX=-122.5 EndY=-209 EndZ=0
    g20: LineSegment StartX=-122.5 StartY=-209 StartZ=0 EndX=-167.5 EndY=-209 EndZ=0
    g21: LineSegment StartX=-167.5 StartY=-209 StartZ=0 EndX=-167.5 EndY=-215 EndZ=0
    g22: LineSegment StartX=-167.5 StartY=-215 StartZ=0 EndX=-212.5 EndY=-215 EndZ=0
    g23: LineSegment StartX=-212.5 StartY=-215 StartZ=0 EndX=-212.5 EndY=-209 EndZ=0
    g24: LineSegment StartX=-212.5 StartY=-209 StartZ=0 EndX=-257.5 EndY=-209 EndZ=0
    g25: LineSegment StartX=-257.5 StartY=-209 StartZ=0 EndX=-257.5 EndY=-215 EndZ=0
    g26: LineSegment StartX=-257.5 StartY=-215 StartZ=0 EndX=-295 EndY=-215 EndZ=0
    g27: LineSegment StartX=-295 StartY=-215 StartZ=0 EndX=-295 EndY=-177.5 EndZ=0
    g28: LineSegment StartX=-295 StartY=-177.5 StartZ=0 EndX=-289 EndY=-177.5 EndZ=0
    g29: LineSegment StartX=-289 StartY=-177.5 StartZ=0 EndX=-289 EndY=-132.5 EndZ=0
    g30: LineSegment StartX=-289 StartY=-132.5 StartZ=0 EndX=-295 EndY=-132.5 EndZ=0
    g31: LineSegment StartX=-295 StartY=-132.5 StartZ=0 EndX=-295 EndY=-87.5 EndZ=0
    g32: LineSegment StartX=-295 StartY=-87.5 StartZ=0 EndX=-289 EndY=-87.5 EndZ=0
    g33: LineSegment StartX=-289 StartY=-87.5 StartZ=0 EndX=-289 EndY=-42.5 EndZ=0
    g34: LineSegment StartX=-289 StartY=-42.5 StartZ=0 EndX=-295 EndY=-42.5 EndZ=0
    g35: LineSegment StartX=-295 StartY=-42.5 StartZ=0 EndX=-295 EndY=-5 EndZ=0
    g36: Circle CenterX=-190 CenterY=-110 CenterZ=0 NormalX=0 NormalY=0 NormalZ=1 Radius=6
    g37: Circle CenterX=-174.444 CenterY=-94.4437 CenterZ=0 NormalX=0 NormalY=0 NormalZ=1 Radius=2
    g38: Circle CenterX=-205.556 CenterY=-94.4437 CenterZ=0 NormalX=0 NormalY=0 NormalZ=1 Radius=2
    g39: Circle CenterX=-205.556 CenterY=-125.556 CenterZ=0 NormalX=0 NormalY=0 NormalZ=1 Radius=2
    g40: Circle CenterX=-174.444 CenterY=-125.556 CenterZ=0 NormalX=0 NormalY=0 NormalZ=1 Radius=2
    g41: LineSegment StartX=-275 StartY=-155 StartZ=0 EndX=-258 EndY=-155 EndZ=0
    g42: LineSegment StartX=-258 StartY=-155 StartZ=0 EndX=-258 EndY=-100 EndZ=0
    g43: LineSegment StartX=-258 StartY=-100 StartZ=0 EndX=-275 EndY=-100 EndZ=0
    g44: LineSegment StartX=-275 StartY=-100 StartZ=0 EndX=-275 EndY=-155 EndZ=0
    g45: Circle CenterX=-266.5 CenterY=-178.5 CenterZ=0 NormalX=0 NormalY=0 NormalZ=1 Radius=2.5
    g46: Circle CenterX=-266.5 CenterY=-163.5 CenterZ=0 NormalX=0 NormalY=0 NormalZ=1 Radius=2.5
    g47: GeomPoint [constr] X=-266.5 Y=-110 Z=0
    g48: LineSegment StartX=-190.528 StartY=-168 StartZ=0 EndX=-135.528 EndY=-168 EndZ=0
    g49: LineSegment StartX=-135.528 StartY=-168 StartZ=0 EndX=-135.528 EndY=-185 EndZ=0
    g50: LineSegment StartX=-135.528 StartY=-185 StartZ=0 EndX=-190.528 EndY=-185 EndZ=0
    g51: LineSegment StartX=-190.528 StartY=-185 StartZ=0 EndX=-190.528 EndY=-168 EndZ=0
    g52: Circle CenterX=-199.028 CenterY=-176.5 CenterZ=0 NormalX=0 NormalY=0 NormalZ=1 Radius=2.5
    g53: Circle CenterX=-214.028 CenterY=-176.5 CenterZ=0 NormalX=0 NormalY=0 NormalZ=1 Radius=2.5
    g54: GeomPoint [constr] X=-145.528 Y=-176.5 Z=0
    g55: LineSegment StartX=-190.528 StartY=-35 StartZ=0 EndX=-135.528 EndY=-35 EndZ=0
    g56: LineSegment StartX=-135.528 StartY=-35 StartZ=0 EndX=-135.528 EndY=-52 EndZ=0
    g57: LineSegment StartX=-135.528 StartY=-52 StartZ=0 EndX=-190.528 EndY=-52 EndZ=0
    g58: LineSegment StartX=-190.528 StartY=-52 StartZ=0 EndX=-190.528 EndY=-35 EndZ=0
    g59: Circle CenterX=-199.028 CenterY=-43.5 CenterZ=0 NormalX=0 NormalY=0 NormalZ=1 Radius=2.5
    g60: Circle CenterX=-214.028 CenterY=-43.5 CenterZ=0 NormalX=0 NormalY=0 NormalZ=1 Radius=2.5
    g61: GeomPoint [constr] X=-145.528 Y=-43.5 Z=0
    g62: Circle CenterX=-101 CenterY=-60 CenterZ=0 NormalX=0 NormalY=0 NormalZ=1 Radius=2
    g63: Circle CenterX=-101 CenterY=-160 CenterZ=0 NormalX=0 NormalY=0 NormalZ=1 Radius=2
  constraints (187):
    c: Horizontal(g0)
    c: Coincident(g0,g1)
    c: Coincident(g1,g2)
    c: Horizontal(g2)
    c: Coincident(g2,g3)
    c: Vertical(g3)
    c: Coincident(g3,g4)
    c: Horizontal(g4)
    c: Coincident(g4,g5)
    c: Vertical(g5)
    c: Coincident(g5,g6)
    c: Horizontal(g6)
    c: Coincident(g6,g7)
    c: Vertical(g7)
    c: Coincident(g7,g8)
    c: Horizontal(g8)
    c: Coincident(g8,g9)
    c: Vertical(g9)
    c: Coincident(g9,g10)
    c: Horizontal(g10)
    c: Coincident(g10,g11)
    c: Vertical(g11)
    c: Coincident(g11,g12)
    c: Horizontal(g12)
    c: Coincident(g12,g13)
    c: Vertical(g13)
    c: Coincident(g13,g14)
    c: Horizontal(g14)
    c: Coincident(g14,g15)
    c: Vertical(g15)
    c: Coincident(g15,g16)
    c: Horizontal(g16)
    c: Coincident(g16,g17)
    c: Vertical(g17)
    c: Coincident(g17,g18)
    c: Horizontal(g18)
    c: Coincident(g18,g19)
    c: Vertical(g19)
    c: Coincident(g19,g20)
    c: Horizontal(g20)
    c: Coincident(g20,g21)
    c: Vertical(g21)
    c: Coincident(g21,g22)
    c: Horizontal(g22)
    c: Coincident(g22,g23)
    c: Vertical(g23)
    c: Coincident(g23,g24)
    c: Horizontal(g24)
    c: Coincident(g24,g25)
    c: Vertical(g25)
    c: Coincident(g25,g26)
    c: Horizontal(g26)
    c: Coincident(g26,g27)
    c: Vertical(g27)
    c: Coincident(g27,g28)
    c: Horizontal(g28)
    c: Coincident(g28,g29)
    c: Vertical(g29)
    c: Coincident(g29,g30)
    c: Horizontal(g30)
    c: Coincident(g30,g31)
    c: Vertical(g31)
    c: Coincident(g31,g32)
    c: Horizontal(g32)
    c: Coincident(g32,g33)
    c: Vertical(g33)
    c: Coincident(g33,g34)
    c: Horizontal(g34)
    c: Coincident(g34,g35)
    c: Coincident(g35,g0)
    c: Vertical(g35)
    c: Vertical(g1)
    c: DistanceX(g4,g4) = 45
    c: DistanceX(g2,g2) = 45
    c: DistanceX(g6,g6) = 45
    c: DistanceY(g11,g11) = 45
    c: DistanceY(g13,g13) = 45
    c: DistanceY(g15,g15) = 45
    c: DistanceX(g20,g20) = 45
    c: DistanceX(g22,g22) = 45
    c: DistanceX(g24,g24) = 45
    c: DistanceY(g29,g29) = 45
    c: DistanceY(g31,g31) = 45
    c: DistanceY(g33,g33) = 45
    c: DistanceY(g1,g1) = 6
    c: DistanceY(g3,g3) = 6
    c: DistanceY(g5,g5) = 6
    c: DistanceX(g10,g10) = 6
    c: DistanceX(g12,g12) = 6
    c: DistanceX(g14,g14) = 6
    c: DistanceX(g16,g16) = 6
    c: DistanceY(g7,g7) = 6
    c: DistanceY(g19,g19) = 6
    c: DistanceY(g21,g21) = 6
    c: DistanceY(g23,g23) = 6
    c: DistanceY(g25,g25) = 6
    c: DistanceX(g28,g28) = 6
    c: DistanceX(g30,g30) = 6
    c: DistanceX(g32,g32) = 6
    c: DistanceX(g34,g34) = 6
    c: DistanceY(g35,g35) = 37.5
    c: DistanceY(g27,g27) = 37.5
    c: DistanceX(g26,g26) = 37.5
    c: DistanceX(g18,g18) = 37.5
    c: DistanceY(g17,g17) = 37.5
    c: DistanceX(g8,g8) = 37.5
    c: DistanceX(g8,g-1) = 85
    c: DistanceY(g8,g-1) = 5
    c: Radius(g36) = 6
    c: Radius(g38) = 2
    c: Radius(g37) = 2
    c: Radius(g40) = 2
    c: Radius(g39) = 2
    c: DistanceY(g40,g39) = 0
    c: Symmetric(g37,g39,g36)
    c: Symmetric(g38,g40,g36)
    c: Distance(g40,g38) = 44
    c: DistanceY(g36,g0) = 105
    c: DistanceX(g0,g36) = 105
    c: Coincident(g41,g42)
    c: Coincident(g42,g43)
    c: Coincident(g43,g44)
    c: Coincident(g44,g41)
    c: Horizontal(g41)
    c: Horizontal(g43)
    c: Vertical(g42)
    c: Vertical(g44)
    c: DistanceX(g43,g43) = 17
    c: DistanceX(g43,g47) = 8.5
    c: DistanceY(g47,g43) = 10
    c: DistanceY(g42,g42) = 55
    c: DistanceY(g47,g0) = 105
    c: Radius(g45) = 2.5
    c: Radius(g46) = 2.5
    c: DistanceX(g0,g43) = 20
    c: DistanceY(g45,g46) = 15
    c: DistanceY(g45,g47) = 68.5
    c: Coincident(g48,g49)
    c: Coincident(g49,g50)
    c: Coincident(g50,g51)
    c: Coincident(g51,g48)
    c: Horizontal(g48)
    c: Horizontal(g50)
    c: Vertical(g49)
    c: Vertical(g51)
    c: Radius(g53) = 2.5
    c: Radius(g52) = 2.5
    c: DistanceX(g53,g52) = 15
    c: DistanceX(g48,g48) = 55
    c: DistanceY(g49,g49) = 17
    c: DistanceY(g17,g49) = 30
    c: DistanceX(g54,g48) = 10
    c: DistanceY(g54,g48) = 8.5
    c: DistanceX(g53,g54) = 68.5
    c: Coincident(g55,g56)
    c: Coincident(g56,g57)
    c: Coincident(g57,g58)
    c: Coincident(g58,g55)
    c: Horizontal(g55)
    c: Horizontal(g57)
    c: Vertical(g56)
    c: Vertical(g58)
    c: DistanceX(g55,g55) = 55
    c: DistanceY(g56,g56) = 17
    c: DistanceY(g55,g8) = 30
    c: Radius(g59) = 2.5
    c: Radius(g60) = 2.5
    c: DistanceX(g60,g59) = 15
    c: DistanceX(g61,g55) = 10
    c: DistanceY(g61,g55) = 8.5
    c: DistanceY(g59,g55) = 8.5
    c: DistanceY(g60,g55) = 8.5
    c: DistanceX(g60,g61) = 68.5
    c: Distance(g37,g39) = 44
    c: Radius(g62) = 2
    c: Radius(g63) = 2
    c: DistanceY(g63,g14) = 27.5
    c: DistanceX(g63,g14) = 10
    c: DistanceY(g11,g62) = 27.5
    c: DistanceX(g62,g11) = 10
    c: DistanceY(g39,g38) = 31.1127
    c: DistanceY(g49,g52) = 8.5
    c: DistanceY(g49,g53) = 8.5
    c: DistanceX(g41,g46) = 8.5
    c: DistanceX(g41,g45) = 8.5
    c: Distance(g36,g61) = 80
    c: Distance(g54,g36) = 80
FEATURE [Sketcher::SketchObject] Sketch007  label="BASE_PAROI_MALE_LCD"
  expr: Constraints[53] = (prefs001.pcbheated - 4 - 2 * prefs001.plexi - 3 * prefs001.top_encoche) / 2
  expr: Constraints[55] = prefs001.side_encoche
  expr: Constraints[108] = prefs001.plexi
  expr: Constraints[59] = (prefs001.box_height - prefs001.side_encoche) / 2
  expr: Constraints[101] = prefs001.big_encoche - 20
  expr: Constraints[52] = (prefs001.pcbheated - 4 - prefs001.big_encoche - 2 * prefs001.plexi) / 2
  expr: Constraints[114] = prefs001.side_encoche
  expr: Constraints[58] = (prefs001.box_height - prefs001.side_encoche) / 2
  expr: Constraints[104] = (prefs001.big_encoche - 55) / 2
  expr: Constraints[66] = prefs001.plexi
  expr: Constraints[116] = prefs001.plexi
  expr: Constraints[38] = prefs001.top_encoche
  expr: Constraints[50] = prefs001.big_encoche
  expr: Constraints[60] = prefs001.plexi
  expr: Constraints[105] = prefs001.LCDcover_encoche
  expr: Constraints[63] = prefs001.plexi
  expr: Constraints[62] = prefs001.plexi
  expr: Constraints[102] = prefs001.plexi
  expr: Constraints[37] = prefs001.top_encoche
  expr: Constraints[106] = prefs001.plexi_LCDcover
  expr: Constraints[111] = prefs001.plexi
  expr: Constraints[115] = (prefs001.pcbheated - 4 - prefs001.LCDcover_encoche - 2 * prefs001.plexi) / 2
  expr: Constraints[65] = prefs001.plexi
  expr: Constraints[112] = prefs001.plexi
  expr: Constraints[64] = prefs001.plexi
  expr: Constraints[117] = (prefs001.pcbheated - 4 - 2 * prefs001.plexi - 3 * prefs001.top_encoche) / 2
  expr: Constraints[61] = prefs001.plexi
  expr: Constraints[54] = prefs001.side_encoche
  expr: Constraints[110] = prefs001.side_encoche
  expr: Constraints[51] = (prefs001.pcbheated - 4 - prefs001.big_encoche - 2 * prefs001.plexi) / 2
  expr: Constraints[118] = prefs001.top_encoche
  expr: Constraints[56] = (prefs001.box_height - prefs001.side_encoche) / 2
  expr: Constraints[57] = (prefs001.box_height - prefs001.side_encoche) / 2
  sketch-geometry (40):
    g0: LineSegment StartX=20 StartY=60 StartZ=0 EndX=81.5 EndY=60 EndZ=0
    g1: LineSegment StartX=81.5 StartY=60 StartZ=0 EndX=81.5 EndY=54 EndZ=0
    g2: LineSegment StartX=81.5 StartY=54 StartZ=0 EndX=156.5 EndY=54 EndZ=0
    g3: LineSegment StartX=156.5 StartY=54 StartZ=0 EndX=156.5 EndY=60 EndZ=0
    g4: LineSegment StartX=156.5 StartY=60 StartZ=0 EndX=218 EndY=60 EndZ=0
    g5: LineSegment StartX=218 StartY=60 StartZ=0 EndX=218 EndY=81 EndZ=0
    g6: LineSegment StartX=218 StartY=81 StartZ=0 EndX=224 EndY=81 EndZ=0
    g7: LineSegment StartX=224 StartY=81 StartZ=0 EndX=224 EndY=97 EndZ=0
    g8: LineSegment StartX=224 StartY=97 StartZ=0 EndX=218 EndY=97 EndZ=0
    g9: LineSegment StartX=218 StartY=97 StartZ=0 EndX=218 EndY=118 EndZ=0
    g10: LineSegment StartX=218 StartY=118 StartZ=0 EndX=186.5 EndY=118 EndZ=0
    g11: LineSegment StartX=186.5 StartY=118 StartZ=0 EndX=186.5 EndY=124 EndZ=0
    g12: LineSegment StartX=186.5 StartY=124 StartZ=0 EndX=141.5 EndY=124 EndZ=0
    g13: LineSegment StartX=141.5 StartY=124 StartZ=0 EndX=141.5 EndY=118 EndZ=0
    g14: LineSegment StartX=141.5 StartY=118 StartZ=0 EndX=96.5 EndY=118 EndZ=0
    g15: LineSegment StartX=96.5 StartY=118 StartZ=0 EndX=96.5 EndY=124 EndZ=0
    g16: LineSegment StartX=96.5 StartY=124 StartZ=0 EndX=51.5 EndY=124 EndZ=0
    g17: LineSegment StartX=51.5 StartY=124 StartZ=0 EndX=51.5 EndY=118 EndZ=0
    g18: LineSegment StartX=51.5 StartY=118 StartZ=0 EndX=20 EndY=118 EndZ=0
    g19: LineSegment StartX=20 StartY=118 StartZ=0 EndX=20 EndY=97 EndZ=0
    g20: LineSegment StartX=20 StartY=97 StartZ=0 EndX=14 EndY=97 EndZ=0
    g21: LineSegment StartX=14 StartY=97 StartZ=0 EndX=14 EndY=81 EndZ=0
    g22: LineSegment StartX=14 StartY=81 StartZ=0 EndX=20 EndY=81 EndZ=0
    g23: LineSegment StartX=20 StartY=81 StartZ=0 EndX=20 EndY=60 EndZ=0
    g24: LineSegment StartX=91.5 StartY=66 StartZ=0 EndX=146.5 EndY=66 EndZ=0
    g25: LineSegment StartX=146.5 StartY=66 StartZ=0 EndX=146.5 EndY=60 EndZ=0
    g26: LineSegment StartX=146.5 StartY=60 StartZ=0 EndX=91.5 EndY=60 EndZ=0
    g27: LineSegment StartX=91.5 StartY=60 StartZ=0 EndX=91.5 EndY=66 EndZ=0
    g28: LineSegment StartX=55 StartY=88 StartZ=0 EndX=183 EndY=88 EndZ=0
    g29: LineSegment StartX=183 StartY=88 StartZ=0 EndX=183 EndY=92 EndZ=0
    g30: LineSegment StartX=183 StartY=92 StartZ=0 EndX=55 EndY=92 EndZ=0
    g31: LineSegment StartX=55 StartY=92 StartZ=0 EndX=55 EndY=88 EndZ=0
    g32: LineSegment StartX=189 StartY=82 StartZ=0 EndX=183 EndY=82 EndZ=0
    g33: LineSegment StartX=183 StartY=82 StartZ=0 EndX=183 EndY=76 EndZ=0
    g34: LineSegment StartX=183 StartY=76 StartZ=0 EndX=189 EndY=76 EndZ=0
    g35: LineSegment StartX=189 StartY=76 StartZ=0 EndX=189 EndY=82 EndZ=0
    g36: LineSegment StartX=55 StartY=82 StartZ=0 EndX=49 EndY=82 EndZ=0
    g37: LineSegment StartX=49 StartY=82 StartZ=0 EndX=49 EndY=76 EndZ=0
    g38: LineSegment StartX=49 StartY=76 StartZ=0 EndX=55 EndY=76 EndZ=0
    g39: LineSegment StartX=55 StartY=76 StartZ=0 EndX=55 EndY=82 EndZ=0
  constraints (120):
    c: Horizontal(g0)
    c: Coincident(g0,g1)
    c: Vertical(g1)
    c: Coincident(g1,g2)
    c: Horizontal(g2)
    c: Coincident(g2,g3)
    c: Vertical(g3)
    c: Coincident(g3,g4)
    c: Horizontal(g4)
    c: Coincident(g4,g5)
    c: Vertical(g5)
    c: Coincident(g5,g6)
    c: Horizontal(g6)
    c: Coincident(g6,g7)
    c: Vertical(g7)
    c: Coincident(g7,g8)
    c: Horizontal(g8)
    c: Coincident(g8,g9)
    c: Vertical(g9)
    c: Coincident(g9,g10)
    c: Horizontal(g10)
    c: Coincident(g10,g11)
    c: Vertical(g11)
    c: Coincident(g11,g12)
    c: Horizontal(g12)
    c: Coincident(g12,g13)
    c: Vertical(g13)
    c: Coincident(g13,g14)
    c: Horizontal(g14)
    c: Coincident(g14,g15)
    c: Vertical(g15)
    c: Coincident(g15,g16)
    c: Horizontal(g16)
    c: Coincident(g16,g17)
    c: Vertical(g17)
    c: Coincident(g17,g18)
    c: Horizontal(g18)
    c: DistanceX(g12,g12) = 45
    c: DistanceX(g14,g14) = 45
    c: Coincident(g18,g19)
    c: Vertical(g19)
    c: Coincident(g19,g20)
    c: Horizontal(g20)
    c: Coincident(g20,g21)
    c: Vertical(g21)
    c: Coincident(g21,g22)
    c: Horizontal(g22)
    c: Coincident(g22,g23)
    c: Coincident(g23,g0)
    c: Vertical(g23)
    c: DistanceX(g2,g2) = 75
    c: DistanceX(g4,g4) = 61.5
    c: DistanceX(g0,g0) = 61.5
    c: DistanceX(g10,g10) = 31.5
    c: DistanceY(g21,g21) = 16
    c: DistanceY(g7,g7) = 16
    c: DistanceY(g9,g9) = 21
    c: DistanceY(g5,g5) = 21
    c: DistanceY(g19,g19) = 21
    c: DistanceY(g23,g23) = 21
    c: DistanceX(g20,g20) = 6
    c: DistanceX(g22,g22) = 6
    c: DistanceY(g17,g17) = 6
    c: DistanceY(g15,g15) = 6
    c: DistanceY(g13,g13) = 6
    c: DistanceY(g11,g11) = 6
    c: DistanceX(g8,g8) = 6
    c: DistanceY(g3,g3) = 6
    c: DistanceY(g-1,g0) = 60
    c: Coincident(g24,g25)
    c: Coincident(g25,g26)
    c: Coincident(g26,g27)
    c: Coincident(g27,g24)
    c: Horizontal(g24)
    c: Horizontal(g26)
    c: Vertical(g25)
    c: Vertical(g27)
    c: Coincident(g28,g29)
    c: Coincident(g29,g30)
    c: Coincident(g30,g31)
    c: Coincident(g31,g28)
    c: Horizontal(g28)
    c: Horizontal(g30)
    c: Vertical(g29)
    c: Vertical(g31)
    c: Coincident(g32,g33)
    c: Coincident(g33,g34)
    c: Coincident(g34,g35)
    c: Coincident(g35,g32)
    c: Horizontal(g32)
    c: Horizontal(g34)
    c: Vertical(g33)
    c: Vertical(g35)
    c: Coincident(g36,g37)
    c: Coincident(g37,g38)
    c: Coincident(g38,g39)
    c: Coincident(g39,g36)
    c: Horizontal(g36)
    c: Horizontal(g38)
    c: Vertical(g37)
    c: Vertical(g39)
    c: DistanceX(g24,g24) = 55
    c: DistanceY(g25,g25) = 6
    c: DistanceY(g0,g26) = 0
    c: DistanceX(g0,g26) = 10
    c: DistanceX(g30,g30) = 128
    c: DistanceY(g29,g29) = 4
    c: DistanceY(g35,g35) = 6
    c: DistanceX(g34,g34) = 6
    c: DistanceX(g32,g28) = 0
    c: DistanceY(g4,g34) = 16
    c: DistanceY(g37,g37) = 6
    c: DistanceX(g36,g36) = 6
    c: DistanceX(g36,g28) = 0
    c: DistanceY(g0,g38) = 16
    c: DistanceX(g18,g30) = 35
    c: DistanceY(g36,g28) = 6
    c: DistanceX(g18,g18) = 31.5
    c: DistanceX(g16,g16) = 45
    c: DistanceX(g-1,g0) = 20
FEATURE [Sketcher::SketchObject] Sketch008  label="BASE_PAROI_LCD1"
  expr: Constraints[29] = prefs001.lcd_length / 2
  expr: Constraints[25] = prefs001.LCDside_encoche
  expr: Constraints[28] = prefs001.lcd_length / 2
  expr: Constraints[26] = prefs001.plexi
  expr: Constraints[30] = prefs001.lcd_length - prefs001.plexi
  expr: Constraints[27] = prefs001.plexi
  expr: Constraints[24] = prefs001.LCDside_encoche + prefs001.plexi
  expr: Constraints[31] = prefs001.side_encoche
  expr: Constraints[33] = prefs001.plexi
  expr: Constraints[32] = prefs001.plexi
  sketch-geometry (12):
    g0: LineSegment StartX=-43 StartY=101 StartZ=0 EndX=-78 EndY=101 EndZ=0
    g1: LineSegment StartX=-78 StartY=101 StartZ=0 EndX=-78 EndY=117 EndZ=0
    g2: LineSegment StartX=-78 StartY=117 StartZ=0 EndX=-84 EndY=117 EndZ=0
    g3: LineSegment StartX=-84 StartY=117 StartZ=0 EndX=-84 EndY=123 EndZ=0
    g4: LineSegment StartX=-84 StartY=123 StartZ=0 EndX=-78 EndY=123 EndZ=0
    g5: LineSegment StartX=-78 StartY=123 StartZ=0 EndX=-78 EndY=129 EndZ=0
    g6: LineSegment StartX=-78 StartY=129 StartZ=0 EndX=-14 EndY=129 EndZ=0
    g7: LineSegment StartX=-14 StartY=129 StartZ=0 EndX=-14 EndY=115 EndZ=0
    g8: LineSegment StartX=-14 StartY=115 StartZ=0 EndX=-8 EndY=115 EndZ=0
    g9: LineSegment StartX=-8 StartY=115 StartZ=0 EndX=-8 EndY=95 EndZ=0
    g10: LineSegment StartX=-8 StartY=95 StartZ=0 EndX=-43 EndY=95 EndZ=0
    g11: LineSegment StartX=-43 StartY=95 StartZ=0 EndX=-43 EndY=101 EndZ=0
  constraints (36):
    c: Horizontal(g0)
    c: Coincident(g0,g1)
    c: Vertical(g1)
    c: Coincident(g1,g2)
    c: Horizontal(g2)
    c: Coincident(g2,g3)
    c: Vertical(g3)
    c: Coincident(g3,g4)
    c: Horizontal(g4)
    c: Coincident(g4,g5)
    c: Vertical(g5)
    c: Coincident(g5,g6)
    c: Horizontal(g6)
    c: Coincident(g6,g7)
    c: Vertical(g7)
    c: Coincident(g7,g8)
    c: Horizontal(g8)
    c: Coincident(g8,g9)
    c: Vertical(g9)
    c: Coincident(g9,g10)
    c: Horizontal(g10)
    c: Coincident(g10,g11)
    c: Coincident(g11,g0)
    c: Vertical(g11)
    c: DistanceY(g9,g9) = 20
    c: DistanceY(g7,g7) = 14
    c: DistanceX(g8,g8) = 6
    c: DistanceY(g11,g11) = 6
    c: DistanceX(g10,g10) = 35
    c: DistanceX(g0,g0) = 35
    c: DistanceX(g6,g6) = 64
    c: DistanceY(g1,g1) = 16
    c: DistanceX(g2,g2) = 6
    c: DistanceY(g3,g3) = 6
    c: DistanceX(g9,g-1) = 8
    c: DistanceY(g-1,g9) = 95
FEATURE [Sketcher::SketchObject] Sketch009  label="BASE_PAROI_LCD2"
  expr: Constraints[23] = prefs001.lcd_length - prefs001.plexi
  expr: Constraints[25] = prefs001.LCDside_encoche
  expr: Constraints[31] = prefs001.side_encoche
  expr: Constraints[29] = prefs001.lcd_length / 2
  expr: Constraints[26] = prefs001.LCDside_encoche + prefs001.plexi
  expr: Constraints[28] = prefs001.lcd_length / 2
  sketch-geometry (12):
    g0: LineSegment StartX=-90 StartY=95 StartZ=0 EndX=-125 EndY=95 EndZ=0
    g1: LineSegment StartX=-125 StartY=95 StartZ=0 EndX=-125 EndY=101 EndZ=0
    g2: LineSegment StartX=-125 StartY=101 StartZ=0 EndX=-160 EndY=101 EndZ=0
    g3: LineSegment StartX=-160 StartY=101 StartZ=0 EndX=-160 EndY=117 EndZ=0
    g4: LineSegment StartX=-160 StartY=117 StartZ=0 EndX=-166 EndY=117 EndZ=0
    g5: LineSegment StartX=-166 StartY=117 StartZ=0 EndX=-166 EndY=123 EndZ=0
    g6: LineSegment StartX=-166 StartY=123 StartZ=0 EndX=-160 EndY=123 EndZ=0
    g7: LineSegment StartX=-160 StartY=123 StartZ=0 EndX=-160 EndY=129 EndZ=0
    g8: LineSegment StartX=-160 StartY=129 StartZ=0 EndX=-96 EndY=129 EndZ=0
    g9: LineSegment StartX=-96 StartY=129 StartZ=0 EndX=-96 EndY=115 EndZ=0
    g10: LineSegment StartX=-96 StartY=115 StartZ=0 EndX=-90 EndY=115 EndZ=0
    g11: LineSegment StartX=-90 StartY=115 StartZ=0 EndX=-90 EndY=95 EndZ=0
  constraints (36):
    c: Horizontal(g0)
    c: Coincident(g0,g1)
    c: Vertical(g1)
    c: Coincident(g1,g2)
    c: Horizontal(g2)
    c: Coincident(g2,g3)
    c: Vertical(g3)
    c: Coincident(g3,g4)
    c: Horizontal(g4)
    c: Coincident(g4,g5)
    c: Vertical(g5)
    c: Coincident(g5,g6)
    c: Coincident(g6,g7)
    c: Vertical(g7)
    c: Coincident(g7,g8)
    c: Horizontal(g8)
    c: Coincident(g8,g9)
    c: Vertical(g9)
    c: Coincident(g9,g10)
    c: Horizontal(g10)
    c: Coincident(g10,g11)
    c: Vertical(g11)
    c: Horizontal(g6)
    c: DistanceX(g8,g8) = 64
    c: DistanceX(g10,g10) = 6
    c: DistanceY(g9,g9) = 14
    c: DistanceY(g11,g11) = 20
    c: Coincident(g0,g11)
    c: DistanceX(g0,g0) = 35
    c: DistanceX(g2,g2) = 35
    c: DistanceY(g1,g1) = 6
    c: DistanceY(g3,g3) = 16
    c: DistanceY(g5,g5) = 6
    c: DistanceX(g4,g4) = 6
    c: DistanceX(g0,g-1) = 90
    c: DistanceY(g-1,g0) = 95
FEATURE [Sketcher::SketchObject] Sketch010  label="BASE_LCD_PAROI_MALE"
  expr: Constraints[24] = prefs001.LCDbottom_encoche
  expr: Constraints[31] = prefs001.plexi
  expr: Constraints[33] = prefs001.plexi
  expr: Constraints[32] = prefs001.plexi
  expr: Constraints[27] = prefs001.LCDside_encoche
  expr: Constraints[30] = prefs001.LCDside_encoche
  expr: Constraints[29] = prefs001.LCDside_encoche
  expr: Constraints[26] = (prefs001.pcbheated - 4 - 2 * prefs001.plexi - 2 * prefs001.lcd2side - prefs001.LCDbottom_encoche) / 2
  expr: Constraints[28] = prefs001.LCDside_encoche
  expr: Constraints[25] = (prefs001.pcbheated - 4 - 2 * prefs001.plexi - 2 * prefs001.lcd2side - prefs001.LCDbottom_encoche) / 2
  sketch-geometry (16):
    g0: LineSegment StartX=15 StartY=130 StartZ=0 EndX=156 EndY=130 EndZ=0
    g1: LineSegment StartX=156 StartY=130 StartZ=0 EndX=156 EndY=144 EndZ=0
    g2: LineSegment StartX=156 StartY=144 StartZ=0 EndX=150 EndY=144 EndZ=0
    g3: LineSegment StartX=150 StartY=144 StartZ=0 EndX=150 EndY=158 EndZ=0
    g4: LineSegment StartX=150 StartY=158 StartZ=0 EndX=109 EndY=158 EndZ=0
    g5: LineSegment StartX=109 StartY=158 StartZ=0 EndX=109 EndY=164 EndZ=0
    g6: LineSegment StartX=109 StartY=164 StartZ=0 EndX=62 EndY=164 EndZ=0
    g7: LineSegment StartX=62 StartY=164 StartZ=0 EndX=62 EndY=158 EndZ=0
    g8: LineSegment StartX=62 StartY=158 StartZ=0 EndX=21 EndY=158 EndZ=0
    g9: LineSegment StartX=21 StartY=158 StartZ=0 EndX=21 EndY=144 EndZ=0
    g10: LineSegment StartX=21 StartY=144 StartZ=0 EndX=15 EndY=144 EndZ=0
    g11: LineSegment StartX=15 StartY=144 StartZ=0 EndX=15 EndY=130 EndZ=0
    g12: LineSegment StartX=32 StartY=153 StartZ=0 EndX=45 EndY=153 EndZ=0
    g13: LineSegment StartX=45 StartY=153 StartZ=0 EndX=45 EndY=145 EndZ=0
    g14: LineSegment StartX=45 StartY=145 StartZ=0 EndX=32 EndY=145 EndZ=0
    g15: LineSegment StartX=32 StartY=145 StartZ=0 EndX=32 EndY=153 EndZ=0
  constraints (48):
    c: Horizontal(g0)
    c: Coincident(g0,g1)
    c: Vertical(g1)
    c: Coincident(g1,g2)
    c: Horizontal(g2)
    c: Coincident(g2,g3)
    c: Vertical(g3)
    c: Coincident(g3,g4)
    c: Horizontal(g4)
    c: Coincident(g4,g5)
    c: Vertical(g5)
    c: Coincident(g5,g6)
    c: Horizontal(g6)
    c: Coincident(g6,g7)
    c: Vertical(g7)
    c: Coincident(g7,g8)
    c: Horizontal(g8)
    c: Coincident(g8,g9)
    c: Vertical(g9)
    c: Coincident(g9,g10)
    c: Horizontal(g10)
    c: Coincident(g10,g11)
    c: Coincident(g11,g0)
    c: Vertical(g11)
    c: DistanceX(g6,g6) = 47
    c: DistanceX(g8,g8) = 41
    c: DistanceX(g4,g4) = 41
    c: DistanceY(g9,g9) = 14
    c: DistanceY(g11,g11) = 14
    c: DistanceY(g3,g3) = 14
    c: DistanceY(g1,g1) = 14
    c: DistanceX(g2,g2) = 6
    c: DistanceY(g5,g5) = 6
    c: DistanceX(g10,g10) = 6
    c: DistanceX(g-1,g0) = 15
    c: DistanceY(g-1,g0) = 130
    c: Coincident(g12,g13)
    c: Coincident(g13,g14)
    c: Coincident(g14,g15)
    c: Coincident(g15,g12)
    c: Horizontal(g12)
    c: Horizontal(g14)
    c: Vertical(g13)
    c: Vertical(g15)
    c: DistanceY(g15,g15) = 8
    c: DistanceX(g14,g14) = 13
    c: DistanceY(g12,g7) = 5
    c: DistanceX(g10,g12) = 17
FEATURE [Sketcher::SketchObject] Sketch011  label="BASE_COUVERCLE_LCD"
  expr: Constraints[21] = prefs001.plexi
  expr: Constraints[20] = prefs001.plexi
  sketch-geometry (9):
    g0: LineSegment StartX=320 StartY=3 StartZ=0 EndX=320 EndY=143 EndZ=0
    g1: LineSegment StartX=320 StartY=143 StartZ=0 EndX=250 EndY=143 EndZ=0
    g2: LineSegment StartX=250 StartY=143 StartZ=0 EndX=250 EndY=137 EndZ=0
    g3: LineSegment StartX=250 StartY=137 StartZ=0 EndX=244 EndY=137 EndZ=0
    g4: LineSegment StartX=244 StartY=137 StartZ=0 EndX=244 EndY=9 EndZ=0
    g5: LineSegment StartX=244 StartY=9 StartZ=0 EndX=250 EndY=9 EndZ=0
    g6: LineSegment StartX=250 StartY=9 StartZ=0 EndX=250 EndY=3 EndZ=0
    g7: LineSegment StartX=250 StartY=3 StartZ=0 EndX=320 EndY=3 EndZ=0
    g8: Circle CenterX=283 CenterY=22 CenterZ=0 NormalX=0 NormalY=0 NormalZ=1 Radius=3.5
  constraints (27):
    c: Vertical(g0)
    c: Coincident(g0,g1)
    c: Coincident(g1,g2)
    c: Vertical(g2)
    c: Coincident(g2,g3)
    c: Horizontal(g3)
    c: Coincident(g3,g4)
    c: Vertical(g4)
    c: Coincident(g4,g5)
    c: Horizontal(g5)
    c: Coincident(g5,g6)
    c: Vertical(g6)
    c: Coincident(g6,g7)
    c: Coincident(g7,g0)
    c: Horizontal(g7)
    c: Horizontal(g1)
    c: DistanceY(g0,g0) = 140
    c: DistanceY(g4,g4) = 128
    c: DistanceX(g1,g1) = 70
    c: DistanceX(g7,g7) = 70
    c: DistanceY(g2,g2) = 6
    c: DistanceX(g3,g3) = 6
    c: DistanceX(g0,g-1) = -320
    c: DistanceY(g-1,g0) = 3
    c: Radius(g8) = 3.5
    c: DistanceY(g6,g8) = 19
    c: DistanceX(g8,g0) = 37
FEATURE [Sketcher::SketchObject] Sketch012  label="BASE_PAROI_FEMELLE_SIDE002"
  expr: Constraints[71] = prefs001.pcbheated + 20
  expr: Constraints[70] = (prefs001.pcbheated - 4 - 3 * prefs001.top_encoche) / 2
  expr: Constraints[52] = (prefs001.box_height - prefs001.side_encoche) / 2
  expr: Constraints[58] = prefs001.plexi
  expr: Constraints[68] = prefs001.top_encoche
  expr: Constraints[67] = prefs001.top_encoche
  expr: Constraints[66] = prefs001.plexi
  expr: Constraints[65] = prefs001.plexi
  expr: Constraints[64] = prefs001.plexi
  expr: Constraints[61] = prefs001.plexi
  expr: Constraints[54] = (prefs001.box_height - prefs001.side_encoche) / 2
  expr: Constraints[63] = prefs001.plexi
  expr: Constraints[62] = prefs001.plexi
  expr: Constraints[59] = prefs001.plexi
  expr: Constraints[55] = prefs001.side_encoche
  expr: Constraints[53] = (prefs001.box_height - prefs001.side_encoche) / 2
  expr: Constraints[51] = (prefs001.box_height - prefs001.side_encoche) / 2
  expr: Constraints[49] = (prefs001.pcbheated - 4 - prefs001.big_encoche) / 2
  expr: Constraints[69] = prefs001.top_encoche
  expr: Constraints[60] = prefs001.plexi
  expr: Constraints[50] = prefs001.side_encoche
  expr: Constraints[46] = prefs001.big_encoche
  sketch-geometry (24):
    g0: LineSegment StartX=-230 StartY=-234 StartZ=0 EndX=-162.5 EndY=-234 EndZ=0
    g1: LineSegment StartX=-162.5 StartY=-234 StartZ=0 EndX=-162.5 EndY=-228 EndZ=0
    g2: LineSegment StartX=-162.5 StartY=-228 StartZ=0 EndX=-87.5 EndY=-228 EndZ=0
    g3: LineSegment StartX=-87.5 StartY=-228 StartZ=0 EndX=-87.5 EndY=-234 EndZ=0
    g4: LineSegment StartX=-87.5 StartY=-234 StartZ=0 EndX=-20 EndY=-234 EndZ=0
    g5: LineSegment StartX=-20 StartY=-234 StartZ=0 EndX=-20 EndY=-255 EndZ=0
    g6: LineSegment StartX=-20 StartY=-255 StartZ=0 EndX=-26 EndY=-255 EndZ=0
    g7: LineSegment StartX=-26 StartY=-255 StartZ=0 EndX=-26 EndY=-271 EndZ=0
    g8: LineSegment StartX=-26 StartY=-271 StartZ=0 EndX=-20 EndY=-271 EndZ=0
    g9: LineSegment StartX=-20 StartY=-271 StartZ=0 EndX=-20 EndY=-292 EndZ=0
    g10: LineSegment StartX=-20 StartY=-292 StartZ=0 EndX=-57.5 EndY=-292 EndZ=0
    g11: LineSegment StartX=-57.5 StartY=-292 StartZ=0 EndX=-57.5 EndY=-298 EndZ=0
    g12: LineSegment StartX=-57.5 StartY=-298 StartZ=0 EndX=-102.5 EndY=-298 EndZ=0
    g13: LineSegment StartX=-102.5 StartY=-298 StartZ=0 EndX=-102.5 EndY=-292 EndZ=0
    g14: LineSegment StartX=-102.5 StartY=-292 StartZ=0 EndX=-147.5 EndY=-292 EndZ=0
    g15: LineSegment StartX=-147.5 StartY=-292 StartZ=0 EndX=-147.5 EndY=-298 EndZ=0
    g16: LineSegment StartX=-147.5 StartY=-298 StartZ=0 EndX=-192.5 EndY=-298 EndZ=0
    g17: LineSegment StartX=-192.5 StartY=-298 StartZ=0 EndX=-192.5 EndY=-292 EndZ=0
    g18: LineSegment StartX=-192.5 StartY=-292 StartZ=0 EndX=-230 EndY=-292 EndZ=0
    g19: LineSegment StartX=-230 StartY=-292 StartZ=0 EndX=-230 EndY=-271 EndZ=0
    g20: LineSegment StartX=-230 StartY=-271 StartZ=0 EndX=-224 EndY=-271 EndZ=0
    g21: LineSegment StartX=-224 StartY=-271 StartZ=0 EndX=-224 EndY=-255 EndZ=0
    g22: LineSegment StartX=-224 StartY=-255 StartZ=0 EndX=-230 EndY=-255 EndZ=0
    g23: LineSegment StartX=-230 StartY=-255 StartZ=0 EndX=-230 EndY=-234 EndZ=0
  constraints (72):
    c: Horizontal(g0)
    c: Coincident(g0,g1)
    c: Vertical(g1)
    c: Coincident(g1,g2)
    c: Horizontal(g2)
    c: Coincident(g2,g3)
    c: Vertical(g3)
    c: Coincident(g3,g4)
    c: Horizontal(g4)
    c: Coincident(g4,g5)
    c: Vertical(g5)
    c: Coincident(g5,g6)
    c: Horizontal(g6)
    c: Coincident(g6,g7)
    c: Vertical(g7)
    c: Coincident(g7,g8)
    c: Horizontal(g8)
    c: Coincident(g8,g9)
    c: Vertical(g9)
    c: Coincident(g9,g10)
    c: Horizontal(g10)
    c: Coincident(g10,g11)
    c: Coincident(g11,g12)
    c: Horizontal(g12)
    c: Coincident(g12,g13)
    c: Vertical(g13)
    c: Coincident(g13,g14)
    c: Horizontal(g14)
    c: Coincident(g14,g15)
    c: Vertical(g15)
    c: Coincident(g15,g16)
    c: Horizontal(g16)
    c: Coincident(g16,g17)
    c: Coincident(g17,g18)
    c: Horizontal(g18)
    c: Coincident(g18,g19)
    c: Vertical(g19)
    c: Coincident(g19,g20)
    c: Horizontal(g20)
    c: Coincident(g20,g21)
    c: Vertical(g21)
    c: Coincident(g21,g22)
    c: Horizontal(g22)
    c: Coincident(g22,g23)
    c: Vertical(g23)
    c: Coincident(g0,g23)
    c: DistanceX(g2,g2) = 75
    c: DistanceX(g0,g0) = 67.5
    c: DistanceX(g-1,g0) = -230
    c: DistanceX(g4,g4) = 67.5
    c: DistanceY(g21,g21) = 16
    c: DistanceY(g23,g23) = 21
    c: DistanceY(g19,g19) = 21
    c: DistanceY(g5,g5) = 21
    c: DistanceY(g9,g9) = 21
    c: DistanceY(g7,g7) = 16
    c: Vertical(g17)
    c: Vertical(g11)
    c: DistanceX(g22,g22) = 6
    c: DistanceX(g20,g20) = 6
    c: DistanceY(g1,g1) = 6
    c: DistanceY(g3,g3) = 6
    c: DistanceX(g6,g6) = 6
    c: DistanceX(g8,g8) = 6
    c: DistanceY(g11,g11) = 6
    c: DistanceY(g13,g13) = 6
    c: DistanceY(g15,g15) = 6
    c: DistanceX(g16,g16) = 45
    c: DistanceX(g12,g12) = 45
    c: DistanceX(g14,g14) = 45
    c: DistanceX(g18,g18) = 37.5
    c: DistanceY(g0,g-1) = 234
FEATURE [Sketcher::SketchObject] Sketch013  label="BASE_JUPE_MALE001"
  expr: Constraints[17] = prefs001.pcbheated
  expr: Constraints[18] = prefs001.plexi * 2
  expr: Constraints[20] = prefs001.plexi * 2
  expr: Constraints[33] = prefs001.plexi * 2
  expr: Constraints[23] = prefs001.plexi * 2
  expr: Constraints[22] = prefs001.plexi
  expr: Constraints[24] = prefs001.plexi * 2
  expr: Constraints[35] = prefs001.pcbheated
  sketch-geometry (12):
    g0: LineSegment StartX=230 StartY=182 StartZ=0 EndX=236 EndY=182 EndZ=0
    g1: LineSegment StartX=236 StartY=182 StartZ=0 EndX=236 EndY=194 EndZ=0
    g2: LineSegment StartX=236 StartY=194 StartZ=0 EndX=230 EndY=194 EndZ=0
    g3: LineSegment StartX=230 StartY=194 StartZ=0 EndX=230 EndY=206 EndZ=0
    g4: LineSegment StartX=230 StartY=206 StartZ=0 EndX=16 EndY=206 EndZ=0
    g5: LineSegment StartX=16 StartY=206 StartZ=0 EndX=16 EndY=194 EndZ=0
    g6: LineSegment StartX=16 StartY=194 StartZ=0 EndX=10 EndY=194 EndZ=0
    g7: LineSegment StartX=10 StartY=194 StartZ=0 EndX=10 EndY=182 EndZ=0
    g8: LineSegment StartX=10 StartY=182 StartZ=0 EndX=16 EndY=182 EndZ=0
    g9: LineSegment StartX=16 StartY=182 StartZ=0 EndX=16 EndY=170 EndZ=0
    g10: LineSegment StartX=16 StartY=170 StartZ=0 EndX=230 EndY=170 EndZ=0
    g11: LineSegment StartX=230 StartY=170 StartZ=0 EndX=230 EndY=182 EndZ=0
  constraints (36):
    c: Horizontal(g0)
    c: Vertical(g1)
    c: Horizontal(g2)
    c: Vertical(g3)
    c: Horizontal(g4)
    c: Vertical(g5)
    c: Vertical(g7)
    c: DistanceX(g-1,g7) = 10
    c: Coincident(g7,g6)
    c: Coincident(g7,g8)
    c: Coincident(g0,g1)
    c: Coincident(g2,g1)
    c: Coincident(g2,g3)
    c: Coincident(g3,g4)
    c: Coincident(g5,g4)
    c: Coincident(g5,g6)
    c: Horizontal(g8)
    c: DistanceX(g4,g4) = 214
    c: DistanceY(g5,g5) = 12
    c: Horizontal(g6)
    c: DistanceY(g7,g7) = 12
    c: DistanceX(g8,g8) = 6
    c: DistanceX(g6,g6) = 6
    c: DistanceY(g3,g3) = 12
    c: DistanceY(g1,g1) = 12
    c: DistanceX(g2,g2) = 6
    c: Vertical(g9)
    c: Coincident(g9,g10)
    c: Horizontal(g10)
    c: Coincident(g10,g11)
    c: Coincident(g11,g0)
    c: Vertical(g11)
    c: Coincident(g9,g8)
    c: DistanceY(g9,g9) = 12
    c: DistanceY(g-1,g9) = 170
    c: DistanceX(g10,g10) = 214
FEATURE [Sketcher::SketchObject] Sketch014  label="BASE_JUPE_FEMELLE001"
  expr: Constraints[37] = prefs001.plexi
  expr: Constraints[34] = prefs001.plexi * 2
  expr: Constraints[33] = prefs001.plexi * 2
  expr: Constraints[11] = prefs001.plexi
  expr: Constraints[36] = prefs001.plexi
  expr: Constraints[31] = prefs001.pcbheated + 2 * prefs001.plexi
  sketch-geometry (14):
    g0: LineSegment StartX=-236 StartY=152 StartZ=0 EndX=-230 EndY=152 EndZ=0
    g1: LineSegment StartX=-230 StartY=152 StartZ=0 EndX=-230 EndY=164 EndZ=0
    g2: LineSegment StartX=-230 StartY=164 StartZ=0 EndX=-236 EndY=164 EndZ=0
    g3: LineSegment StartX=-236 StartY=164 StartZ=0 EndX=-236 EndY=175 EndZ=0
    g4: LineSegment StartX=-196 StartY=215 StartZ=0 EndX=-50 EndY=215 EndZ=0
    g5: LineSegment StartX=-16 StartY=164 StartZ=0 EndX=-16 EndY=152 EndZ=0
    g6: ArcOfCircle CenterX=-50 CenterY=175 CenterZ=0 NormalX=0 NormalY=0 NormalZ=1 Radius=40 StartAngle=6.28318 EndAngle=7.85398
    g7: ArcOfCircle CenterX=-196 CenterY=175 CenterZ=0 NormalX=0 NormalY=0 NormalZ=1 Radius=40 StartAngle=1.5708 EndAngle=3.14159
    g8: LineSegment StartX=-16 StartY=164 StartZ=0 EndX=-10 EndY=164 EndZ=0
    g9: LineSegment StartX=-10 StartY=175 StartZ=0 EndX=-10 EndY=164 EndZ=0
    g10: LineSegment StartX=-236 StartY=152 StartZ=0 EndX=-236 EndY=140 EndZ=0
    g11: LineSegment StartX=-236 StartY=140 StartZ=0 EndX=-10 EndY=140 EndZ=0
    g12: LineSegment StartX=-10 StartY=140 StartZ=0 EndX=-10 EndY=152 EndZ=0
    g13: LineSegment StartX=-10 StartY=152 StartZ=0 EndX=-16 EndY=152 EndZ=0
  constraints (41):
    c: Horizontal(g0)
    c: Coincident(g0,g1)
    c: Vertical(g1)
    c: Coincident(g1,g2)
    c: Horizontal(g2)
    c: Coincident(g2,g3)
    c: Vertical(g3)
    c: Horizontal(g4)
    c: Vertical(g5)
    c: DistanceY(g1,g1) = 12
    c: DistanceY(g5,g5) = 12
    c: DistanceX(g2,g2) = 6
    c: DistanceX(g0,g0) = 6
    c: Tangent(g4,g6) = 1.5708
    c: Tangent(g3,g7) = 1.5708
    c: Tangent(g4,g7) = 1.5708
    c: Radius(g7) = 40
    c: Radius(g6) = 40
    c: Coincident(g8,g5)
    c: Horizontal(g8)
    c: Coincident(g9,g6)
    c: Coincident(g9,g8)
    c: Vertical(g9)
    c: Vertical(g10)
    c: Coincident(g10,g11)
    c: Horizontal(g11)
    c: Coincident(g11,g12)
    c: Vertical(g12)
    c: Coincident(g12,g13)
    c: Coincident(g13,g5)
    c: Horizontal(g13)
    c: DistanceX(g11,g11) = 226
    c: DistanceY(g10,g4) = 75
    c: DistanceY(g10,g10) = 12
    c: DistanceY(g12,g12) = 12
    c: Coincident(g0,g10)
    c: DistanceX(g8,g8) = 6
    c: DistanceX(g13,g13) = 6
    c: DistanceY(g-1,g11) = 140
    c: DistanceX(g11,g-1) = 10
    c: Tangent(g6,g9)
FEATURE [Sketcher::SketchObject] Sketch015  label="BASE_PAROI_MALE_BACK001"
  expr: Constraints[111] = prefs001.power_height
  expr: Constraints[110] = prefs001.power_length
  expr: Constraints[107] = prefs001.ethernet_height
  expr: Constraints[51] = prefs001.side_encoche
  expr: Constraints[106] = prefs001.ethernet_length
  expr: Constraints[104] = prefs001.usb_length
  expr: Constraints[109] = prefs001.ethernet_height
  expr: Constraints[53] = prefs001.top_encoche
  expr: Constraints[108] = prefs001.ethernet_length
  expr: Constraints[59] = (prefs001.box_height - prefs001.side_encoche) / 2
  expr: Constraints[55] = prefs001.top_encoche
  expr: Constraints[43] = prefs001.big_encoche
  expr: Constraints[48] = (prefs001.pcbheated - 4 - prefs001.big_encoche - 2 * prefs001.plexi) / 2
  expr: Constraints[62] = prefs001.plexi
  expr: Constraints[69] = prefs001.plexi
  expr: Constraints[49] = (prefs001.pcbheated - 4 - prefs001.big_encoche - 2 * prefs001.plexi) / 2
  expr: Constraints[56] = (prefs001.box_height - prefs001.side_encoche) / 2
  expr: Constraints[67] = prefs001.plexi
  expr: Constraints[57] = (prefs001.box_height - prefs001.side_encoche) / 2
  expr: Constraints[58] = (prefs001.box_height - prefs001.side_encoche) / 2
  expr: Constraints[63] = prefs001.plexi
  expr: Constraints[64] = prefs001.plexi
  expr: Constraints[61] = (prefs001.pcbheated - 4 - 3 * prefs001.top_encoche - 2 * prefs001.plexi) / 2
  expr: Constraints[54] = prefs001.top_encoche
  expr: Constraints[65] = prefs001.plexi
  expr: Constraints[66] = prefs001.plexi
  expr: Constraints[68] = prefs001.plexi
  expr: Constraints[105] = prefs001.usb_height
  expr: Constraints[50] = prefs001.side_encoche
  expr: Constraints[60] = (prefs001.pcbheated - 4 - 3 * prefs001.top_encoche - 2 * prefs001.plexi) / 2
  sketch-geometry (41):
    g0: LineSegment StartX=-330 StartY=-208 StartZ=0 EndX=-351 EndY=-208 EndZ=0
    g1: LineSegment StartX=-351 StartY=-208 StartZ=0 EndX=-351 EndY=-214 EndZ=0
    g2: LineSegment StartX=-351 StartY=-214 StartZ=0 EndX=-367 EndY=-214 EndZ=0
    g3: LineSegment StartX=-367 StartY=-214 StartZ=0 EndX=-367 EndY=-208 EndZ=0
    g4: LineSegment StartX=-367 StartY=-208 StartZ=0 EndX=-388 EndY=-208 EndZ=0
    g5: LineSegment StartX=-388 StartY=-208 StartZ=0 EndX=-388 EndY=-176.5 EndZ=0
    g6: LineSegment StartX=-388 StartY=-176.5 StartZ=0 EndX=-394 EndY=-176.5 EndZ=0
    g7: LineSegment StartX=-394 StartY=-176.5 StartZ=0 EndX=-394 EndY=-131.5 EndZ=0
    g8: LineSegment StartX=-394 StartY=-131.5 StartZ=0 EndX=-388 EndY=-131.5 EndZ=0
    g9: LineSegment StartX=-388 StartY=-131.5 StartZ=0 EndX=-388 EndY=-86.5 EndZ=0
    g10: LineSegment StartX=-388 StartY=-86.5 StartZ=0 EndX=-394 EndY=-86.5 EndZ=0
    g11: LineSegment StartX=-394 StartY=-86.5 StartZ=0 EndX=-394 EndY=-41.5 EndZ=0
    g12: LineSegment StartX=-394 StartY=-41.5 StartZ=0 EndX=-388 EndY=-41.5 EndZ=0
    g13: LineSegment StartX=-388 StartY=-41.5 StartZ=0 EndX=-388 EndY=-10 EndZ=0
    g14: LineSegment StartX=-367 StartY=-10 StartZ=0 EndX=-367 EndY=-4 EndZ=0
    g15: LineSegment StartX=-367 StartY=-4 StartZ=0 EndX=-351 EndY=-4 EndZ=0
    g16: LineSegment StartX=-351 StartY=-4 StartZ=0 EndX=-351 EndY=-10 EndZ=0
    g17: LineSegment StartX=-388 StartY=-10 StartZ=0 EndX=-367 EndY=-10 EndZ=0
    g18: LineSegment StartX=-351 StartY=-10 StartZ=0 EndX=-330 EndY=-10 EndZ=0
    g19: LineSegment StartX=-330 StartY=-10 StartZ=0 EndX=-330 EndY=-71.5 EndZ=0
    g20: LineSegment StartX=-330 StartY=-71.5 StartZ=0 EndX=-324 EndY=-71.5 EndZ=0
    g21: LineSegment StartX=-324 StartY=-71.5 StartZ=0 EndX=-324 EndY=-146.5 EndZ=0
    g22: LineSegment StartX=-324 StartY=-146.5 StartZ=0 EndX=-330 EndY=-146.5 EndZ=0
    g23: LineSegment StartX=-330 StartY=-146.5 StartZ=0 EndX=-330 EndY=-208 EndZ=0
    g24: LineSegment StartX=-346 StartY=-28 StartZ=0 EndX=-341 EndY=-28 EndZ=0
    g25: LineSegment StartX=-341 StartY=-28 StartZ=0 EndX=-341 EndY=-37 EndZ=0
    g26: LineSegment StartX=-341 StartY=-37 StartZ=0 EndX=-346 EndY=-37 EndZ=0
    g27: LineSegment StartX=-346 StartY=-37 StartZ=0 EndX=-346 EndY=-28 EndZ=0
    g28: LineSegment StartX=-357 StartY=-40 StartZ=0 EndX=-341 EndY=-40 EndZ=0
    g29: LineSegment StartX=-341 StartY=-40 StartZ=0 EndX=-341 EndY=-55 EndZ=0
    g30: LineSegment StartX=-341 StartY=-55 StartZ=0 EndX=-357 EndY=-55 EndZ=0
    g31: LineSegment StartX=-357 StartY=-55 StartZ=0 EndX=-357 EndY=-40 EndZ=0
    g32: LineSegment StartX=-357 StartY=-57 StartZ=0 EndX=-341 EndY=-57 EndZ=0
    g33: LineSegment StartX=-341 StartY=-57 StartZ=0 EndX=-341 EndY=-72 EndZ=0
    g34: LineSegment StartX=-341 StartY=-72 StartZ=0 EndX=-357 EndY=-72 EndZ=0
    g35: LineSegment StartX=-357 StartY=-72 StartZ=0 EndX=-357 EndY=-57 EndZ=0
    g36: LineSegment StartX=-353.5 StartY=-75 StartZ=0 EndX=-341 EndY=-75 EndZ=0
    g37: LineSegment StartX=-341 StartY=-75 StartZ=0 EndX=-341 EndY=-85 EndZ=0
    g38: LineSegment StartX=-341 StartY=-85 StartZ=0 EndX=-353.5 EndY=-85 EndZ=0
    g39: LineSegment StartX=-353.5 StartY=-85 StartZ=0 EndX=-353.5 EndY=-75 EndZ=0
    g40: Circle CenterX=-345.5 CenterY=-95 CenterZ=0 NormalX=0 NormalY=0 NormalZ=1 Radius=4.5
  constraints (123):
    c: Horizontal(g0)
    c: Coincident(g0,g1)
    c: Vertical(g1)
    c: Coincident(g1,g2)
    c: Horizontal(g2)
    c: Coincident(g2,g3)
    c: Vertical(g3)
    c: Coincident(g3,g4)
    c: Horizontal(g4)
    c: Coincident(g4,g5)
    c: Vertical(g5)
    c: Coincident(g5,g6)
    c: Horizontal(g6)
    c: Coincident(g6,g7)
    c: Vertical(g7)
    c: Coincident(g7,g8)
    c: Horizontal(g8)
    c: Coincident(g8,g9)
    c: Vertical(g9)
    c: Coincident(g9,g10)
    c: Horizontal(g10)
    c: Coincident(g10,g11)
    c: Vertical(g11)
    c: Coincident(g11,g12)
    c: Coincident(g12,g13)
    c: Vertical(g13)
    c: Vertical(g14)
    c: Coincident(g14,g15)
    c: Horizontal(g15)
    c: Coincident(g15,g16)
    c: Vertical(g16)
    c: Coincident(g17,g13)
    c: Coincident(g17,g14)
    c: Coincident(g18,g16)
    c: Horizontal(g18)
    c: Vertical(g19)
    c: Horizontal(g20)
    c: Coincident(g21,g20)
    c: Vertical(g21)
    c: Horizontal(g22)
    c: Coincident(g23,g0)
    c: Vertical(g23)
    c: Horizontal(g17)
    c: DistanceY(g21,g21) = 75
    c: Coincident(g22,g21)
    c: Coincident(g23,g22)
    c: Coincident(g20,g19)
    c: Coincident(g18,g19)
    c: DistanceY(g19,g19) = 61.5
    c: DistanceY(g23,g23) = 61.5
    c: DistanceX(g15,g15) = 16
    c: DistanceX(g2,g2) = 16
    c: Horizontal(g12)
    c: DistanceY(g11,g11) = 45
    c: DistanceY(g9,g9) = 45
    c: DistanceY(g7,g7) = 45
    c: DistanceX(g18,g18) = 21
    c: DistanceX(g17,g17) = 21
    c: DistanceX(g4,g4) = 21
    c: DistanceX(g0,g0) = 21
    c: DistanceY(g13,g13) = 31.5
    c: DistanceY(g5,g5) = 31.5
    c: DistanceY(g14,g14) = 6
    c: DistanceY(g16,g16) = 6
    c: DistanceX(g12,g12) = 6
    c: DistanceX(g10,g10) = 6
    c: DistanceX(g20,g20) = 6
    c: DistanceX(g8,g8) = 6
    c: DistanceX(g6,g6) = 6
    c: DistanceY(g3,g3) = 6
    c: DistanceY(g18,g-1) = 10
    c: DistanceX(g18,g-1) = 330
    c: Coincident(g24,g25)
    c: Coincident(g25,g26)
    c: Coincident(g26,g27)
    c: Coincident(g27,g24)
    c: Horizontal(g24)
    c: Horizontal(g26)
    c: Vertical(g25)
    c: Vertical(g27)
    c: Coincident(g28,g29)
    c: Coincident(g29,g30)
    c: Coincident(g30,g31)
    c: Coincident(g31,g28)
    c: Horizontal(g28)
    c: Horizontal(g30)
    c: Vertical(g29)
    c: Vertical(g31)
    c: Coincident(g32,g33)
    c: Coincident(g33,g34)
    c: Coincident(g34,g35)
    c: Coincident(g35,g32)
    c: Horizontal(g32)
    c: Horizontal(g34)
    c: Vertical(g33)
    c: Vertical(g35)
    c: Coincident(g36,g37)
    c: Coincident(g37,g38)
    c: Coincident(g38,g39)
    c: Coincident(g39,g36)
    c: Horizontal(g36)
    c: Horizontal(g38)
    c: Vertical(g37)
    c: Vertical(g39)
    c: DistanceY(g25,g25) = 9
    c: DistanceX(g24,g24) = 5
    c: DistanceY(g29,g29) = 15
    c: DistanceX(g28,g28) = 16
    c: DistanceY(g33,g33) = 15
    c: DistanceX(g32,g32) = 16
    c: DistanceY(g37,g37) = 10
    c: DistanceX(g38,g38) = 12.5
    c: DistanceX(g24,g18) = 11
    c: DistanceX(g25,g28) = 0
    c: DistanceX(g29,g32) = 0
    c: DistanceX(g33,g36) = 0
    c: DistanceY(g28,g25) = 3
    c: DistanceY(g32,g29) = 2
    c: DistanceY(g36,g33) = 3
    c: DistanceY(g24,g18) = 18
    c: Radius(g40) = 4.5
    c: DistanceX(g40,g37) = 4.5
    c: DistanceY(g40,g37) = 10
